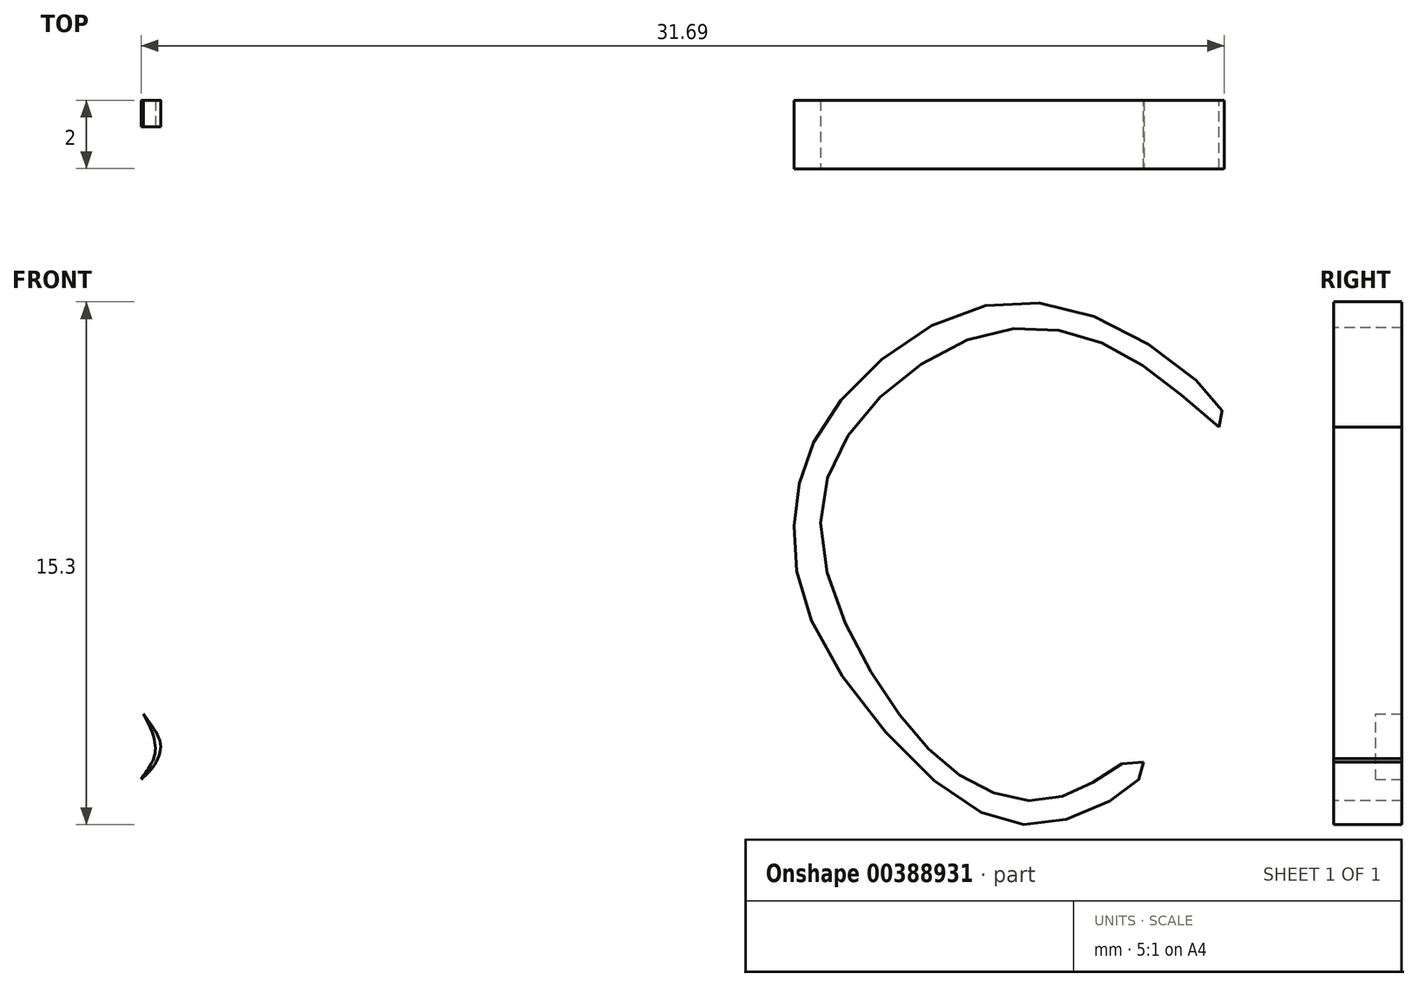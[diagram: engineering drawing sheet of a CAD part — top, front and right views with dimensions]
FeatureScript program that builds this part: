
annotation { "Feature Type Name" : "Feature", "Feature Type Description" : "" }
export const myFeature = defineFeature(function(context is Context, id is Id, definition is map)
    precondition{}
    {
        {
            var Q0;
            Q0=qCreatedBy(makeId("Front.planeOp"),FACE);
            var sketch = newSketch(context, id + "F0", { "sketchPlane" : qUnion([Q0])});
            skArc(sketch, "E0", {"start": v(-3.69, -6.27) * mm, "mid": v(-3.7, -6.14) * mm, "end": v(-3.75, -6.03) * mm});
            skArc(sketch, "E1", {"start": v(3.08, -7.56) * mm, "mid": v(3.43, -7.14) * mm, "end": v(3.75, -6.7) * mm});
            skArc(sketch, "E2", {"start": v(0.71, -7.74) * mm, "mid": v(1.48, -8.13) * mm, "end": v(2.34, -8.08) * mm});
            skArc(sketch, "E3", {"start": v(0.71, -7.74) * mm, "mid": v(-1.43, -7) * mm, "end": v(-3.66, -7.38) * mm});
            skArc(sketch, "E4", {"start": v(-3.75, -7.3) * mm, "mid": v(-3.7, -6.94) * mm, "end": v(-3.68, -6.58) * mm});
            skArc(sketch, "E5", {"start": v(-3.68, -6.58) * mm, "mid": v(-3.68, -6.42) * mm, "end": v(-3.69, -6.27) * mm});
            skArc(sketch, "E6", {"start": v(2.34, -8.08) * mm, "mid": v(2.75, -7.87) * mm, "end": v(3.08, -7.56) * mm});
            skArc(sketch, "E7", {"start": v(-3.75, -6.03) * mm, "mid": v(-3.11, -4.42) * mm, "end": v(-3.75, -2.81) * mm});
            skArc(sketch, "E8", {"start": v(-4.2, -1.47) * mm, "mid": v(-4.18, -2.2) * mm, "end": v(-3.75, -2.81) * mm});
            skArc(sketch, "E9", {"start": v(-4.2, -1.47) * mm, "mid": v(-4.23, -1.22) * mm, "end": v(-4.45, -1.12) * mm});
            skArc(sketch, "E10", {"start": v(-4.45, -1.12) * mm, "mid": v(-5.42, -1.46) * mm, "end": v(-6.03, -2.29) * mm});
            skArc(sketch, "E11", {"start": v(-6.03, -2.29) * mm, "mid": v(-6.03, -2.9) * mm, "end": v(-5.62, -3.34) * mm});
            skArc(sketch, "E12", {"start": v(-5.58, -3.48) * mm, "mid": v(-5.56, -3.4) * mm, "end": v(-5.62, -3.34) * mm});
            skArc(sketch, "E13", {"start": v(-5.85, -3.54) * mm, "mid": v(-5.7, -3.55) * mm, "end": v(-5.58, -3.48) * mm});
            skArc(sketch, "E14", {"start": v(-6.07, -3.4) * mm, "mid": v(-5.96, -3.48) * mm, "end": v(-5.85, -3.54) * mm});
            skArc(sketch, "E15", {"start": v(-6.07, -3.4) * mm, "mid": v(-6.2, -3.36) * mm, "end": v(-6.33, -3.4) * mm});
            skArc(sketch, "E16", {"start": v(-6.49, -3.4) * mm, "mid": v(-6.4, -3.43) * mm, "end": v(-6.33, -3.4) * mm});
            skArc(sketch, "E17", {"start": v(-6.49, -3.4) * mm, "mid": v(-6.53, -3.4) * mm, "end": v(-6.52, -3.45) * mm});
            skArc(sketch, "E18", {"start": v(-6.44, -3.64) * mm, "mid": v(-6.44, -3.53) * mm, "end": v(-6.52, -3.45) * mm});
            skArc(sketch, "E19", {"start": v(-6.94, -3.71) * mm, "mid": v(-6.68, -3.8) * mm, "end": v(-6.44, -3.64) * mm});
            skArc(sketch, "E20", {"start": v(-6.94, -3.71) * mm, "mid": v(-7, -3.7) * mm, "end": v(-7, -3.77) * mm});
            skArc(sketch, "E21", {"start": v(-6.83, -4.05) * mm, "mid": v(-6.89, -3.9) * mm, "end": v(-7, -3.77) * mm});
            skArc(sketch, "E22", {"start": v(-7, -4.29) * mm, "mid": v(-6.87, -4.2) * mm, "end": v(-6.83, -4.05) * mm});
            skArc(sketch, "E23", {"start": v(-8.44, -3.46) * mm, "mid": v(-7.85, -4.1) * mm, "end": v(-7, -4.29) * mm});
            skArc(sketch, "E24", {"start": v(-8.44, -3.46) * mm, "mid": v(-8.5, -3.42) * mm, "end": v(-8.58, -3.46) * mm});
            skArc(sketch, "E25", {"start": v(-8.58, -3.46) * mm, "mid": v(-8.6, -3.5) * mm, "end": v(-8.6, -3.53) * mm});
            skArc(sketch, "E26", {"start": v(-8.86, -3.73) * mm, "mid": v(-8.7, -3.67) * mm, "end": v(-8.6, -3.53) * mm});
            skArc(sketch, "E27", {"start": v(-10.15, -2.7) * mm, "mid": v(-9.7, -3.46) * mm, "end": v(-8.86, -3.73) * mm});
            skArc(sketch, "E28", {"start": v(-10.15, -1.95) * mm, "mid": v(-10.17, -2.33) * mm, "end": v(-10.15, -2.7) * mm});
            skArc(sketch, "E29", {"start": v(-10.15, -1.95) * mm, "mid": v(-10.19, -1.76) * mm, "end": v(-10.34, -1.64) * mm});
            skArc(sketch, "E30", {"start": v(-10.34, -1.64) * mm, "mid": v(-11.08, -1.57) * mm, "end": v(-11.81, -1.64) * mm});
            skArc(sketch, "E31", {"start": v(-11.81, -1.64) * mm, "mid": v(-12.01, -1.73) * mm, "end": v(-12.18, -1.88) * mm});
            skArc(sketch, "E32", {"start": v(-12.18, -1.88) * mm, "mid": v(-12.35, -2.1) * mm, "end": v(-12.51, -2.35) * mm});
            skArc(sketch, "E33", {"start": v(-13.94, -3.35) * mm, "mid": v(-13.1, -3.05) * mm, "end": v(-12.51, -2.35) * mm});
            skArc(sketch, "E34", {"start": v(-15.03, -2.58) * mm, "mid": v(-14.63, -3.17) * mm, "end": v(-13.94, -3.35) * mm});
            skArc(sketch, "E35", {"start": v(-14.95, -2.18) * mm, "mid": v(-15.04, -2.37) * mm, "end": v(-15.03, -2.58) * mm});
            skArc(sketch, "E36", {"start": v(-14.45, -1.64) * mm, "mid": v(-14.7, -1.9) * mm, "end": v(-14.95, -2.18) * mm});
            skArc(sketch, "E37", {"start": v(-14.45, -1.64) * mm, "mid": v(-14.26, -0.97) * mm, "end": v(-14.63, -0.38) * mm});
            skArc(sketch, "E38", {"start": v(-14.63, -0.38) * mm, "mid": v(-15.23, -0.4) * mm, "end": v(-15.62, -0.85) * mm});
            skArc(sketch, "E39", {"start": v(-16.04, -1.37) * mm, "mid": v(-15.79, -1.14) * mm, "end": v(-15.62, -0.85) * mm});
            skArc(sketch, "E40", {"start": v(-16.04, -1.37) * mm, "mid": v(-16.21, -1.5) * mm, "end": v(-16.36, -1.64) * mm});
            skArc(sketch, "E41", {"start": v(-17.02, -1.64) * mm, "mid": v(-16.69, -1.78) * mm, "end": v(-16.36, -1.64) * mm});
            skArc(sketch, "E42", {"start": v(-17.41, -1.23) * mm, "mid": v(-17.22, -1.44) * mm, "end": v(-17.02, -1.64) * mm});
            skArc(sketch, "E43", {"start": v(-17.89, 0.31) * mm, "mid": v(-17.85, -0.52) * mm, "end": v(-17.41, -1.23) * mm});
            skArc(sketch, "E44", {"start": v(-17.89, 0.31) * mm, "mid": v(-17.89, 0.33) * mm, "end": v(-17.9, 0.34) * mm});
            skArc(sketch, "E45", {"start": v(-17.9, 0.34) * mm, "mid": v(-17.94, 0.33) * mm, "end": v(-17.97, 0.3) * mm});
            skArc(sketch, "E46", {"start": v(-19.3, -0.58) * mm, "mid": v(-18.59, -0.2) * mm, "end": v(-17.97, 0.3) * mm});
            skArc(sketch, "E47", {"start": v(-19.9, -0.65) * mm, "mid": v(-19.6, -0.67) * mm, "end": v(-19.3, -0.58) * mm});
            skArc(sketch, "E48", {"start": v(-20.2, -0.11) * mm, "mid": v(-20.12, -0.42) * mm, "end": v(-19.9, -0.65) * mm});
            skArc(sketch, "E49", {"start": v(-20.2, -0.11) * mm, "mid": v(-20.18, 0.21) * mm, "end": v(-20.2, 0.54) * mm});
            skArc(sketch, "E50", {"start": v(-20.2, 0.54) * mm, "mid": v(-20.43, 1) * mm, "end": v(-20.9, 1.16) * mm});
            skArc(sketch, "E51", {"start": v(-20.9, 1.16) * mm, "mid": v(-22.68, 0.63) * mm, "end": v(-23.68, -0.94) * mm});
            skArc(sketch, "E52", {"start": v(-23.68, -0.94) * mm, "mid": v(-23.57, -1.58) * mm, "end": v(-23.11, -2.05) * mm});
            skArc(sketch, "E53", {"start": v(-22.81, -2.32) * mm, "mid": v(-22.93, -2.15) * mm, "end": v(-23.11, -2.05) * mm});
            skArc(sketch, "E54", {"start": v(-22.81, -2.6) * mm, "mid": v(-22.79, -2.45) * mm, "end": v(-22.81, -2.32) * mm});
            skArc(sketch, "E55", {"start": v(-23.7, -2.5) * mm, "mid": v(-23.28, -2.79) * mm, "end": v(-22.81, -2.6) * mm});
            skArc(sketch, "E56", {"start": v(-23.7, -2.5) * mm, "mid": v(-23.76, -2.37) * mm, "end": v(-23.84, -2.26) * mm});
            skArc(sketch, "E57", {"start": v(-23.84, -2.26) * mm, "mid": v(-23.93, -2.24) * mm, "end": v(-23.97, -2.32) * mm});
            skArc(sketch, "E58", {"start": v(-23.97, -2.32) * mm, "mid": v(-23.9, -2.69) * mm, "end": v(-23.68, -2.99) * mm});
            skArc(sketch, "E59", {"start": v(-23.63, -3.23) * mm, "mid": v(-23.6, -3.1) * mm, "end": v(-23.68, -2.99) * mm});
            skArc(sketch, "E60", {"start": v(-24.4, -3.23) * mm, "mid": v(-24.02, -3.39) * mm, "end": v(-23.63, -3.23) * mm});
            skArc(sketch, "E61", {"start": v(-24.4, -3.23) * mm, "mid": v(-24.46, -3.22) * mm, "end": v(-24.46, -3.28) * mm});
            skArc(sketch, "E62", {"start": v(-24.25, -3.83) * mm, "mid": v(-24.3, -3.54) * mm, "end": v(-24.46, -3.28) * mm});
            skArc(sketch, "E63", {"start": v(-24.88, -3.93) * mm, "mid": v(-24.52, -4.17) * mm, "end": v(-24.25, -3.83) * mm});
            skArc(sketch, "E64", {"start": v(-24.88, -3.93) * mm, "mid": v(-24.9, -3.83) * mm, "end": v(-24.92, -3.72) * mm});
            skArc(sketch, "E65", {"start": v(-24.92, -3.72) * mm, "mid": v(-24.98, -3.67) * mm, "end": v(-25.05, -3.72) * mm});
            skArc(sketch, "E66", {"start": v(-25.05, -3.72) * mm, "mid": v(-24.55, -5.28) * mm, "end": v(-23.07, -6) * mm});
            skArc(sketch, "E67", {"start": v(-23.07, -6) * mm, "mid": v(-22.64, -6) * mm, "end": v(-22.21, -6) * mm});
            skFitSpline(sketch, "E68", {"points": [v(-22.21, -6) * mm, v(-21.9, -5.69) * mm, v(-22.42, -5.12) * mm, v(-20.66, -4.08) * mm, v(-19.53, -4.6) * mm, v(-18.44, -3.59) * mm, v(-17.7, -3.55) * mm, v(-17.3, -4.07) * mm, v(-18.01, -5.15) * mm, v(-18.16, -6.77) * mm, v(-19.58, -7.9) * mm, v(-20.92, -8.76) * mm, v(-19.16, -9.38) * mm, v(-17.63, -11.12) * mm, v(-17.96, -11.4) * mm, v(-18.92, -11.12) * mm, v(-19.35, -11.4) * mm, v(-18.82, -12.21) * mm, v(-18.25, -13.86) * mm, v(-17.89, -14.27) * mm, v(-17.26, -14.18) * mm, v(-17.21, -14.1) * mm, v(-16.82, -13.65) * mm, v(-16.4, -14.93) * mm, v(-15.95, -16.13) * mm, v(-16, -16.67) * mm, v(-16.88, -17.28) * mm, v(-18, -17) * mm, v(-18.67, -16.4) * mm, v(-18.87, -16.58) * mm, v(-20.13, -18.4) * mm, v(-22.21, -18.16) * mm, v(-23.39, -16.7) * mm, v(-22.8, -16) * mm, v(-22.6, -15.5) * mm, v(-21.4, -14.67) * mm, v(-20.45, -15.27) * mm, v(-20.4, -15.2) * mm, v(-19.55, -14.57) * mm, v(-19.55, -14.51) * mm, v(-20.24, -12.1) * mm, v(-21.74, -9.86) * mm, v(-21.89, -10) * mm, v(-22.57, -11.73) * mm, v(-24.55, -12.05) * mm, v(-25.57, -11.22) * mm, v(-25.52, -10.76) * mm, v(-24.63, -10.83) * mm, v(-23.99, -10.75) * mm, v(-23.57, -10.3) * mm, v(-23.62, -9.63) * mm, v(-24.39, -9.1) * mm, v(-24.85, -8.06) * mm, v(-24.99, -7.7) * mm, v(-25.33, -7.6) * mm, v(-25.79, -8.16) * mm, v(-26.7, -8.35) * mm, v(-26.98, -8) * mm, v(-26.47, -7.58) * mm, v(-25.9, -6.57) * mm, v(-26.59, -5.35) * mm, v(-26.9, -3.41) * mm, v(-26.66, -1.41) * mm, v(-26.1, -0.15) * mm, v(-26.15, -0.1) * mm, v(-26.98, -0.1) * mm, v(-27.86, 1) * mm, v(-27.19, 1.9) * mm, v(-26.36, 1.09) * mm, v(-25.57, 0.89) * mm, v(-24.93, 1.43) * mm, v(-25.03, 2.07) * mm, v(-24.98, 2.4) * mm, v(-24.52, 2.24) * mm, v(-23.77, 2.17) * mm, v(-23.28, 2.53) * mm, v(-23.85, 3.22) * mm, v(-24.88, 4.71) * mm, v(-25.1, 6.85) * mm, v(-24.19, 7.52) * mm, v(-23.42, 7.55) * mm, v(-23.42, 7.81) * mm, v(-22.98, 7.98) * mm, v(-22.02, 7) * mm, v(-21.13, 6.22) * mm, v(-20.8, 6.59) * mm, v(-20.77, 6.92) * mm, v(-20.34, 7.57) * mm, v(-19.35, 7.23) * mm, v(-19.43, 6.54) * mm, v(-19.19, 6) * mm, v(-18.92, 6.15) * mm, v(-18.73, 6.59) * mm, v(-17.48, 5.5) * mm, v(-17.65, 4.85) * mm, v(-17.53, 4.1) * mm, v(-16.28, 3.5) * mm, v(-15.58, 4.1) * mm, v(-15.99, 5.29) * mm, v(-16.18, 7.76) * mm, v(-14.98, 10.1) * mm, v(-14.02, 10.84) * mm, v(-14.04, 10.98) * mm, v(-14.3, 11.2) * mm, v(-14.26, 11.68) * mm, v(-14.9, 12.35) * mm, v(-14.47, 12.76) * mm, v(-14.5, 12.98) * mm, v(-13.31, 13.17) * mm, v(-12.95, 12.98) * mm, v(-12.78, 12.7) * mm, v(-12.5, 12.73) * mm, v(-12.51, 11.57) * mm, v(-12.8, 11.39) * mm, v(-12.87, 11.15) * mm, v(-12.56, 10.86) * mm, v(-12.17, 11.28) * mm, v(-12.07, 11.93) * mm, v(-11.4, 12.97) * mm, v(-10.5, 12.27) * mm, v(-10.81, 11.25) * mm, v(-11.37, 10.8) * mm, v(-11.37, 10.2) * mm, v(-10.6, 9.47) * mm, v(-10.71, 7.65) * mm, v(-11.88, 7.07) * mm, v(-12.68, 7.83) * mm, v(-12.61, 8.84) * mm, v(-12.09, 8.94) * mm, v(-11.99, 8.56) * mm, v(-12.3, 8.34) * mm, v(-12.41, 8.1) * mm, v(-11.92, 7.99) * mm, v(-11.6, 8.77) * mm, v(-11.88, 9.26) * mm, v(-12.97, 9.2) * mm, v(-13.24, 8.02) * mm, v(-12.78, 7.4) * mm, v(-12.99, 7.05) * mm, v(-13.52, 7.56) * mm, v(-13.52, 8.22) * mm, v(-13.79, 8.07) * mm, v(-13.75, 7.4) * mm, v(-13.5, 7.2) * mm, v(-13.74, 6.83) * mm, v(-13.7, 5.91) * mm, v(-13.1, 5.64) * mm, v(-12.67, 6.13) * mm, v(-12.34, 6.25) * mm, v(-12.17, 5.76) * mm, v(-12.27, 5.27) * mm, v(-11.88, 4.76) * mm, v(-11.05, 4.98) * mm, v(-10.8, 4.8) * mm, v(-11.14, 3.82) * mm, v(-10.97, 1.97) * mm, v(-9.55, 0.66) * mm, v(-8.25, 0.7) * mm, v(-7.67, 1.44) * mm, v(-7.7, 2.05) * mm, v(-7.2, 2.2) * mm, v(-7.14, 2.45) * mm, v(-6.68, 2.43) * mm, v(-6.73, 2.87) * mm, v(-6, 3.16) * mm, v(-6.05, 3.53) * mm, v(-5.3, 3.55) * mm, v(-5.16, 3.86) * mm, v(-4.16, 3.78) * mm, v(-3.69, 4.3) * mm, v(-2.67, 4.26) * mm, v(-2.26, 4.35) * mm, v(-2.19, 4.83) * mm, v(-1.73, 4.9) * mm, v(-1.64, 5.52) * mm, v(-2.17, 6.6) * mm, v(-2.43, 7.76) * mm, v(-3.17, 8.62) * mm, v(-3.99, 9.16) * mm, v(-3.79, 9.72) * mm, v(-2.96, 9.77) * mm, v(-2.77, 10.18) * mm, v(-1.46, 10.34) * mm, v(-1.13, 10.32) * mm, v(-1.07, 10.64) * mm, v(-0.66, 10.82) * mm, v(-0.53, 11.1) * mm, v(-0.66, 11.45) * mm, v(-0.53, 11.92) * mm, v(-0.62, 12.39) * mm, v(-1, 12.6) * mm, v(-1.12, 13.07) * mm, v(-1.87, 13.16) * mm, v(-2.38, 13.87) * mm, v(-2.16, 14.67) * mm, v(-2.29, 15.23) * mm, v(-2.8, 15.72) * mm, v(-2.88, 16.93) * mm, v(-2.36, 17.1) * mm, v(-2.01, 18.05) * mm, v(-1.15, 18.93) * mm, v(-1.23, 19.93) * mm, v(-0.72, 20.85) * mm, v(0.24, 20.64) * mm, v(0.5, 19.89) * mm, v(0.83, 19.65) * mm, v(1.03, 20.22) * mm, v(1.62, 20.54) * mm, v(1.85, 21) * mm, v(1.8, 21.4) * mm, v(2.12, 21.8) * mm, v(2.42, 21.23) * mm, v(3.19, 20.8) * mm, v(3.2, 20.38) * mm, v(2.52, 20.42) * mm, v(3.1, 19.8) * mm, v(3.13, 19.02) * mm, v(3.53, 18.64) * mm, v(4.12, 18.7) * mm, v(4.51, 18.33) * mm, v(4.52, 18.01) * mm, v(4.78, 17.78) * mm, v(4.97, 17.45) * mm, v(4.72, 17.03) * mm, v(4.3, 17.17) * mm, v(4.45, 16.92) * mm, v(4.54, 16.54) * mm, v(3.13, 15.18) * mm, v(2.28, 14.96) * mm, v(0.66, 13.16) * mm, v(0.76, 13.02) * mm, v(1.03, 12.76) * mm, v(0.88, 12.47) * mm, v(0.92, 12.05) * mm, v(1.37, 11.9) * mm, v(1.35, 11.58) * mm, v(1.33, 10.63) * mm, v(1.7, 10.73) * mm, v(1.98, 10.37) * mm, v(2.16, 10.19) * mm, v(2.4, 10.37) * mm, v(3.41, 10.27) * mm, v(3.73, 9.64) * mm, v(4.08, 9.72) * mm, v(4.74, 9.68) * mm, v(4.97, 8.61) * mm, v(4.57, 8.22) * mm, v(4.03, 8.32) * mm, v(3.72, 8.02) * mm, v(3.54, 7.54) * mm, v(3.18, 7.18) * mm, v(2.23, 5.35) * mm, v(2.39, 4.4) * mm, v(3.11, 4.19) * mm, v(4.08, 3.58) * mm, v(4.8, 3.55) * mm, v(5.54, 3) * mm, v(5.5, 2.69) * mm, v(5.8, 2.47) * mm, v(7.01, 2.48) * mm, v(7.32, 2.07) * mm, v(7.84, 2) * mm, v(8.06, 1.4) * mm, v(7.9, 1.06) * mm, v(7.96, 0.8) * mm, v(8.38, 0.7) * mm, v(8.6, -0.11) * mm, v(10.91, 0.96) * mm, v(11.66, 2.74) * mm, v(11.15, 3.49) * mm, v(10.93, 4.07) * mm, v(11.8, 4.33) * mm, v(12.5, 3.73) * mm, v(12.69, 3.97) * mm, v(12.73, 4.6) * mm, v(13.15, 4.66) * mm, v(13.15, 5.37) * mm, v(13.6, 5.79) * mm, v(14.02, 4.9) * mm, v(14.19, 5.37) * mm, v(14.49, 5.12) * mm, v(14.6, 6.05) * mm, v(13.86, 6.78) * mm, v(13.68, 6.64) * mm, v(12.65, 6.05) * mm, v(11.52, 6.4) * mm, v(10.95, 7.8) * mm, v(11.66, 9.23) * mm, v(12.18, 9.6) * mm, v(12.29, 10.18) * mm, v(11.98, 10.32) * mm, v(11.78, 10.03) * mm, v(11.54, 10.6) * mm, v(11.72, 12) * mm, v(12.59, 12.4) * mm, v(13.28, 11.71) * mm, v(13.68, 11.35) * mm, v(14.1, 12) * mm, v(15.28, 12.38) * mm, v(16.4, 11.6) * mm, v(16.29, 11.27) * mm, v(15.58, 11.27) * mm, v(15.48, 10.98) * mm, v(15.3, 10.66) * mm, v(15.14, 10.24) * mm, v(15.48, 9.45) * mm], "startDerivative": vector(210.1, 118.94) * mm, "endDerivative": vector(144.38, -239.42) * mm});
            skFitSpline(sketch, "E69", {"points": [v(15.48, 9.45) * mm, v(16.8, 7.3) * mm, v(16.96, 5.4) * mm, v(16.3, 3.59) * mm, v(16.35, 3.18) * mm, v(16.85, 3.1) * mm, v(17.08, 2.8) * mm, v(17.12, 2.56) * mm, v(17.42, 2.7) * mm, v(18.09, 3.7) * mm, v(18.29, 5.04) * mm, v(18.86, 5.75) * mm, v(19.46, 5.33) * mm, v(19.64, 5.02) * mm, v(20.19, 6.03) * mm, v(21.24, 7.1) * mm, v(21.77, 6.62) * mm, v(21.56, 5.95) * mm, v(21.58, 4.92) * mm, v(22.13, 5.08) * mm, v(22.66, 5.08) * mm, v(22.98, 5.69) * mm, v(23.5, 6.01) * mm, v(23.74, 6.45) * mm, v(24.53, 6.73) * mm, v(25.91, 5.3) * mm, v(25.5, 2.83) * mm, v(24.31, 1.79) * mm, v(24.24, 1.39) * mm, v(24.9, 0.9) * mm, v(25.83, -0.16) * mm, v(26.79, -0.67) * mm, v(27.53, -0.46) * mm, v(27.59, 0.06) * mm, v(27.42, 0.32) * mm, v(27.64, 0.67) * mm, v(28.32, -0.13) * mm, v(28.46, -2) * mm, v(27.46, -2.76) * mm, v(26.82, -2.67) * mm, v(26.94, -3.27) * mm, v(27.4, -4.6) * mm, v(27.24, -6.37) * mm, v(26.67, -7.12) * mm, v(26.47, -8.23) * mm, v(26.74, -8.55) * mm, v(26.46, -8.92) * mm, v(26.66, -9.53) * mm, v(27.3, -9.55) * mm, v(27.53, -9.82) * mm, v(26.82, -10.26) * mm, v(25.67, -9.92) * mm, v(25.44, -9.6) * mm, v(25.03, -10) * mm, v(24.01, -10.56) * mm, v(23.93, -11.56) * mm, v(24.74, -12.2) * mm, v(25.59, -11.96) * mm, v(25.93, -12.22) * mm, v(24.21, -13.7) * mm, v(23.4, -14) * mm, v(22.46, -13.52) * mm, v(21.88, -13.18) * mm, v(21.24, -13.52) * mm, v(19.67, -15.94) * mm, v(20.03, -16.27) * mm, v(21.33, -16.04) * mm, v(22.48, -16.32) * mm, v(23.26, -17.58) * mm, v(22.53, -19.4) * mm, v(20.98, -20.28) * mm, v(19.08, -19.65) * mm, v(18.52, -18.7) * mm, v(18.45, -17.92) * mm, v(18.02, -17.58) * mm, v(17.41, -18) * mm, v(17.08, -18) * mm, v(16.84, -17.54) * mm, v(16.64, -17.5) * mm, v(16.34, -17.42) * mm, v(16.22, -16.8) * mm, v(16.47, -16.58) * mm, v(16.27, -16.27) * mm, v(16.45, -15.95) * mm, v(16.64, -16.1) * mm, v(16.85, -15.76) * mm, v(16.5, -15.26) * mm, v(16.98, -14.94) * mm, v(17.44, -15.15) * mm, v(18.85, -13.62) * mm, v(19.01, -12.48) * mm, v(18.65, -12.12) * mm, v(18.15, -12.53) * mm, v(17.41, -12.5) * mm, v(17.54, -11.98) * mm, v(18, -11.68) * mm, v(17.91, -11.3) * mm, v(18.31, -11.12) * mm, v(18.57, -10.9) * mm, v(18.57, -10.25) * mm, v(18.98, -10.28) * mm, v(19.93, -10.63) * mm, v(21.2, -10.3) * mm, v(20.98, -9.68) * mm, v(19.23, -8.79) * mm, v(18.62, -8.26) * mm, v(18.54, -6.5) * mm, v(18.52, -5.52) * mm, v(18.12, -5.27) * mm, v(17.9, -4.97) * mm, v(18.17, -4.52) * mm, v(19, -4.74) * mm, v(19.31, -5.43) * mm, v(19.53, -5.69) * mm, v(19.73, -5.16) * mm, v(20.24, -5.09) * mm, v(20.6, -4.7) * mm, v(21.33, -5.04) * mm, v(22.04, -5.2) * mm, v(22.27, -6) * mm, v(22.06, -6.47) * mm, v(22.46, -7.06) * mm, v(23.74, -6.43) * mm, v(25.24, -4.79) * mm, v(25.14, -4.37) * mm, v(24.71, -4.13) * mm, v(23.97, -4.29) * mm, v(23.3, -4.04) * mm, v(23.37, -3.62) * mm, v(23.88, -3.19) * mm, v(23.21, -1.7) * mm, v(22.06, -0.56) * mm, v(21.31, -0.54) * mm, v(21, -0.96) * mm, v(21.15, -1.57) * mm, v(20.74, -1.94) * mm, v(19.8, -1.86) * mm, v(18.6, -1.21) * mm, v(17.98, -1.06) * mm, v(17.9, -1.66) * mm, v(17.75, -2) * mm, v(17.47, -2.04) * mm, v(15.95, -1.6) * mm, v(15.05, -1.03) * mm, v(14.08, -0.97) * mm, v(13.44, -1.43) * mm, v(14.14, -2.04) * mm, v(15.24, -2.74) * mm, v(15.77, -3.39) * mm, v(15, -3.63) * mm, v(13.15, -3.49) * mm, v(12.06, -2.53) * mm, v(11.76, -1.71) * mm, v(11.28, -1.37) * mm, v(10.53, -1.99) * mm, v(10.3, -3) * mm, v(10.28, -3.82) * mm, v(9.66, -3.83) * mm, v(9.1, -3.29) * mm, v(8.73, -3.69) * mm, v(8.1, -4.29) * mm, v(7.76, -4.46) * mm, v(7.2, -3.77) * mm, v(7.1, -3.27) * mm, v(6.72, -3.59) * mm, v(6.29, -3.86) * mm, v(6, -3.32) * mm, v(6.08, -2.39) * mm, v(5.66, -1.84) * mm, v(4.72, -1.57) * mm, v(2.79, -2.17) * mm, v(1.92, -3.89) * mm, v(2.23, -5.47) * mm, v(3.36, -6.65) * mm, v(3.75, -6.7) * mm], "startDerivative": vector(154.8, -214.57) * mm, "endDerivative": vector(87.05, 10.6) * mm});
            skFitSpline(sketch, "E70", {"points": [v(-1.09, -4.51) * mm, v(-1.2, -4.56) * mm, v(-1.23, -5.16) * mm, v(-1.76, -6.02) * mm, v(-2.78, -6.35) * mm, v(-2.88, -6.46) * mm, v(-2.78, -6.65) * mm, v(-1.6, -6.22) * mm, v(-0.98, -5.4) * mm, v(-0.91, -4.6) * mm, v(-1.09, -4.51) * mm]});
            skFitSpline(sketch, "E71", {"points": [v(-0.08, -4.47) * mm, v(-0.25, -4.57) * mm, v(-0.31, -5.7) * mm, v(0.17, -6.76) * mm, v(1.03, -7.55) * mm, v(1.27, -7.53) * mm, v(1.28, -7.35) * mm, v(0.55, -6.77) * mm, v(-0.07, -5.26) * mm, v(0.14, -4.63) * mm, v(-0.08, -4.47) * mm]});
            skFitSpline(sketch, "E72", {"points": [v(1.1, -2.72) * mm, v(1.06, -2.9) * mm, v(0.2, -3.37) * mm, v(-0.9, -3.19) * mm, v(-2.58, -1.25) * mm, v(-2.82, 0.09) * mm, v(-2.44, 1.18) * mm, v(-0.9, 2.36) * mm, v(0.85, 2.16) * mm, v(2, 1.2) * mm, v(1.95, 1.05) * mm], "startDerivative": vector(0.31, -4.22) * mm, "endDerivative": vector(-3.07, -3.26) * mm});
            skFitSpline(sketch, "E73", {"points": [v(1.95, 1.05) * mm, v(0.67, 1.98) * mm, v(-0.68, 2.1) * mm, v(-2.13, 1.09) * mm, v(-2.52, -0.28) * mm, v(-1.75, -2.04) * mm, v(-0.87, -2.93) * mm, v(-0.02, -3.15) * mm, v(0.68, -2.85) * mm, v(1.1, -2.72) * mm], "startDerivative": vector(-9.7, 8.55) * mm, "endDerivative": vector(3.66, -4.58) * mm});
            skFitSpline(sketch, "E74", {"points": [v(-0.55, -0.47) * mm, v(-0.54, -0.65) * mm, v(-1.62, -0.71) * mm, v(-2.06, -0.38) * mm, v(-2.08, 0.56) * mm, v(-1.25, 1.4) * mm, v(-0.61, 1.47) * mm, v(-0.5, 1.26) * mm, v(-0.81, 1.2) * mm, v(-1.42, 1) * mm, v(-1.86, 0.33) * mm, v(-1.71, -0.38) * mm, v(-1.01, -0.46) * mm, v(-0.55, -0.47) * mm]});
            skFitSpline(sketch, "E75", {"points": [v(0.27, -0.52) * mm, v(0.3, -0.67) * mm, v(0.8, -0.73) * mm, v(2.4, -0.7) * mm, v(2.66, -0.5) * mm, v(2.44, -0.16) * mm, v(1.45, 0.78) * mm, v(0.36, 1.3) * mm, v(0.29, 1.14) * mm, v(0.51, 1.04) * mm, v(1.86, 0.15) * mm, v(2.4, -0.38) * mm, v(2.35, -0.46) * mm, v(0.5, -0.42) * mm, v(0.27, -0.52) * mm]});
            skFitSpline(sketch, "E76", {"points": [v(2.51, 1.91) * mm, v(2.5, 1.8) * mm, v(4.1, 0.16) * mm, v(5.83, -1.16) * mm, v(6.1, -1.22) * mm, v(6.11, -1.1) * mm, v(5.78, -0.87) * mm, v(4.31, 0.24) * mm, v(2.98, 1.58) * mm, v(2.64, 1.98) * mm, v(2.51, 1.91) * mm]});
            skFitSpline(sketch, "E77", {"points": [v(4.13, 1.99) * mm, v(3.97, 1.91) * mm, v(5.08, 0.67) * mm, v(6.37, -0.32) * mm, v(6.6, -0.32) * mm, v(6.6, -0.13) * mm, v(6.48, -0.09) * mm, v(5.2, 0.9) * mm, v(4.3, 1.94) * mm, v(4.13, 1.99) * mm]});
            skFitSpline(sketch, "E78", {"points": [v(1.85, 2.75) * mm, v(1.86, 2.88) * mm, v(2.58, 3.16) * mm, v(4.22, 3.11) * mm, v(4.83, 2.88) * mm, v(4.75, 2.7) * mm, v(4.2, 2.87) * mm, v(2.66, 2.9) * mm, v(1.85, 2.75) * mm]});
            skFitSpline(sketch, "E79", {"points": [v(7.08, 1.97) * mm, v(7.19, 1.84) * mm, v(6.92, 1.56) * mm, v(6.62, 1.66) * mm, v(6.7, 1.82) * mm, v(6.92, 1.83) * mm, v(7.08, 1.97) * mm]});
            skFitSpline(sketch, "E80", {"points": [v(6.31, 1.73) * mm, v(6.33, 1.52) * mm, v(5.63, 1.63) * mm, v(5.2, 1.93) * mm, v(5.22, 2.21) * mm, v(5.37, 2.1) * mm, v(5.83, 1.83) * mm, v(6.31, 1.73) * mm]});
            skFitSpline(sketch, "E81", {"points": [v(-0.6, 3.08) * mm, v(-0.42, 3.1) * mm, v(-0.34, 3.5) * mm, v(0.05, 4.15) * mm, v(0.78, 4.48) * mm, v(1.14, 4.45) * mm, v(1.21, 4.68) * mm, v(0.95, 4.73) * mm, v(0.3, 4.58) * mm, v(-0.46, 3.88) * mm, v(-0.6, 3.08) * mm]});
            skFitSpline(sketch, "E82", {"points": [v(-2.2, 3.49) * mm, v(-2.1, 3.37) * mm, v(-1.88, 3.65) * mm, v(-1.2, 4.34) * mm, v(-0.36, 4.74) * mm, v(-0.23, 4.89) * mm, v(-0.37, 5) * mm, v(-1.52, 4.38) * mm, v(-2.2, 3.49) * mm]});
            skFitSpline(sketch, "E83", {"points": [v(-0.46, 5.42) * mm, v(-0.34, 5.42) * mm, v(-0.33, 6.15) * mm, v(-0.9, 7.93) * mm, v(-1.74, 9.14) * mm, v(-1.93, 9.22) * mm, v(-1.87, 9.01) * mm, v(-1.18, 8) * mm, v(-0.62, 6.27) * mm, v(-0.46, 5.42) * mm]});
            skFitSpline(sketch, "E84", {"points": [v(-0.79, 9.67) * mm, v(-0.6, 9.61) * mm, v(-0.4, 9.16) * mm, v(0.27, 8.77) * mm, v(0.95, 9.18) * mm, v(1.07, 9.73) * mm, v(1.4, 9.6) * mm, v(0.74, 8.65) * mm, v(-0.15, 8.57) * mm, v(-0.73, 9.14) * mm, v(-0.79, 9.67) * mm]});
            skFitSpline(sketch, "E85", {"points": [v(2.15, 9.67) * mm, v(2.25, 9.48) * mm, v(2.06, 9.28) * mm, v(1.17, 7.67) * mm, v(0.8, 5.62) * mm, v(0.66, 5.4) * mm, v(0.54, 5.5) * mm, v(0.85, 7.75) * mm, v(2.15, 9.67) * mm]});
            skFitSpline(sketch, "E86", {"points": [v(1.3, 5.03) * mm, v(1.23, 5.3) * mm, v(1.97, 7.33) * mm, v(3.12, 9.2) * mm, v(3.35, 9.16) * mm, v(3.24, 8.93) * mm, v(2.17, 7.25) * mm, v(1.52, 5.21) * mm, v(1.3, 5.03) * mm]});
            skFitSpline(sketch, "E87", {"points": [v(-6.84, 0.9) * mm, v(-6.67, 1.1) * mm, v(-6.3, 0.99) * mm, v(-4.33, 1.46) * mm, v(-3.08, 2.72) * mm, v(-2.8, 2.95) * mm, v(-2.74, 2.81) * mm, v(-4.16, 1.22) * mm, v(-6.84, 0.9) * mm]});
            skFitSpline(sketch, "E88", {"points": [v(-6.28, -0.29) * mm, v(-6.05, -0.45) * mm, v(-6.25, -0.61) * mm, v(-6.96, -0.85) * mm, v(-7.3, -1.55) * mm, v(-7.49, -1.7) * mm, v(-7.6, -1.52) * mm, v(-7.19, -0.65) * mm, v(-6.28, -0.29) * mm]});
            skFitSpline(sketch, "E89", {"points": [v(-8.79, -3.17) * mm, v(-9, -2.6) * mm, v(-9.02, -1.95) * mm, v(-8.84, -1.83) * mm, v(-8.75, -2.03) * mm, v(-8.7, -2.55) * mm, v(-8.54, -3.05) * mm, v(-8.58, -3.17) * mm, v(-8.79, -3.17) * mm]});
            skFitSpline(sketch, "E90", {"points": [v(-7.6, -2.3) * mm, v(-7.43, -2.4) * mm, v(-7.33, -3) * mm, v(-7.08, -3.47) * mm, v(-7.17, -3.62) * mm, v(-7.59, -3.04) * mm, v(-7.6, -2.3) * mm]});
            skFitSpline(sketch, "E91", {"points": [v(-6.64, -3.17) * mm, v(-6.97, -2.88) * mm, v(-6.98, -2.59) * mm, v(-6.8, -2.75) * mm, v(-6.6, -3) * mm, v(-6.64, -3.17) * mm]});
            skFitSpline(sketch, "E92", {"points": [v(-11.12, -0.31) * mm, v(-10.94, -0.24) * mm, v(-11.03, -0.03) * mm, v(-12.18, 0.21) * mm, v(-13.28, -0.01) * mm, v(-13.38, -0.25) * mm, v(-13.15, -0.34) * mm, v(-12.13, -0.07) * mm, v(-11.12, -0.31) * mm]});
            skFitSpline(sketch, "E93", {"points": [v(-13.72, 4.93) * mm, v(-13.5, 4.7) * mm, v(-13.3, 3.45) * mm, v(-11.76, 1.2) * mm, v(-10.38, 0.43) * mm, v(-10.4, 0.15) * mm, v(-11.92, 1) * mm, v(-13.61, 3.38) * mm, v(-13.72, 4.93) * mm]});
            skFitSpline(sketch, "E94", {"points": [v(-15, 2.95) * mm, v(-14.83, 2.95) * mm, v(-13.64, 1.58) * mm, v(-12.1, 0.7) * mm, v(-11.98, 0.51) * mm, v(-12.16, 0.45) * mm, v(-13.8, 1.43) * mm, v(-15, 2.95) * mm]});
            skFitSpline(sketch, "E95", {"points": [v(-15.1, 4.24) * mm, v(-14.86, 4.18) * mm, v(-14.82, 4.43) * mm, v(-15.3, 6.32) * mm, v(-14.4, 8.95) * mm, v(-12.53, 9.99) * mm, v(-12.4, 10.14) * mm, v(-12.59, 10.31) * mm, v(-14.57, 9.13) * mm, v(-15.58, 6.36) * mm, v(-15.1, 4.24) * mm]});
            skFitSpline(sketch, "E96", {"points": [v(-17.82, 0.47) * mm, v(-17.16, 1.05) * mm, v(-17, 1.11) * mm, v(-16.96, 0.91) * mm, v(-17.82, 0.47) * mm]});
            skFitSpline(sketch, "E97", {"points": [v(-14.63, 1.2) * mm, v(-14.4, 1.24) * mm, v(-14.5, 1.47) * mm, v(-15.83, 1.89) * mm, v(-18.44, 3.44) * mm, v(-19.48, 4.38) * mm, v(-19.75, 4.4) * mm, v(-19.65, 4.2) * mm, v(-18.36, 3.03) * mm, v(-15.9, 1.62) * mm, v(-14.63, 1.2) * mm]});
            skFitSpline(sketch, "E98", {"points": [v(-20.56, 4.12) * mm, v(-20.37, 4.08) * mm, v(-19.54, 3.02) * mm, v(-18.21, 2.21) * mm, v(-18.1, 1.98) * mm, v(-18.4, 1.94) * mm, v(-20.26, 3.5) * mm, v(-20.56, 4.12) * mm]});
            skFitSpline(sketch, "E99", {"points": [v(-20.63, 4.76) * mm, v(-20.6, 4.71) * mm, v(-20.44, 4.78) * mm, v(-20.51, 4.92) * mm, v(-20.5, 5.36) * mm, v(-20.17, 5.47) * mm, v(-20.06, 5.3) * mm, v(-19.98, 5.36) * mm, v(-20.05, 5.7) * mm, v(-20.7, 5.52) * mm, v(-20.63, 4.76) * mm]});
            skFitSpline(sketch, "E100", {"points": [v(-21.45, 4.47) * mm, v(-21.24, 4.45) * mm, v(-21.2, 4.56) * mm, v(-21.3, 4.8) * mm, v(-21.25, 5.4) * mm, v(-20.84, 5.73) * mm, v(-20.92, 5.97) * mm, v(-21.57, 5.4) * mm, v(-21.45, 4.47) * mm]});
            skFitSpline(sketch, "E101", {"points": [v(-23.56, 5.11) * mm, v(-23.33, 5.06) * mm, v(-23.11, 4.6) * mm, v(-22.38, 3.97) * mm, v(-21.38, 3.96) * mm, v(-21.08, 3.95) * mm, v(-21.21, 3.7) * mm, v(-22.32, 3.72) * mm, v(-23.3, 4.4) * mm, v(-23.56, 5.11) * mm]});
            skFitSpline(sketch, "E102", {"points": [v(-22.98, 7.12) * mm, v(-22.85, 6.94) * mm, v(-23.04, 6.77) * mm, v(-23.54, 6.78) * mm, v(-24.04, 6.17) * mm, v(-23.83, 4.81) * mm, v(-22.97, 3.62) * mm, v(-22.03, 3.1) * mm, v(-22.07, 2.88) * mm, v(-23, 3.32) * mm, v(-24.04, 4.63) * mm, v(-24.39, 5.76) * mm, v(-23.95, 6.9) * mm, v(-22.98, 7.12) * mm]});
            skFitSpline(sketch, "E103", {"points": [v(-21.19, 2.6) * mm, v(-20.91, 2.62) * mm, v(-20.88, 2.28) * mm, v(-21.64, 2.17) * mm, v(-23.53, 1.09) * mm, v(-24.85, -0.72) * mm, v(-25.1, -1.26) * mm, v(-25.33, -1.08) * mm, v(-24.7, 0.11) * mm, v(-22.6, 2.13) * mm, v(-21.19, 2.6) * mm]});
            skFitSpline(sketch, "E104", {"points": [v(-24.96, -1.85) * mm, v(-24.75, -2) * mm, v(-24.75, -2.46) * mm, v(-24.55, -2.99) * mm, v(-24.73, -3.16) * mm, v(-25.03, -2.45) * mm, v(-24.96, -1.85) * mm]});
            skFitSpline(sketch, "E105", {"points": [v(-25.74, -2.01) * mm, v(-25.54, -2.23) * mm, v(-25.68, -2.6) * mm, v(-25.62, -4.41) * mm, v(-24.55, -6.1) * mm, v(-23.03, -6.9) * mm, v(-21.5, -6.9) * mm, v(-21.1, -6.99) * mm, v(-21.43, -7.2) * mm, v(-23.2, -7.17) * mm, v(-24.85, -6.16) * mm, v(-25.33, -5.61) * mm, v(-25.33, -6.57) * mm, v(-25.8, -7.39) * mm, v(-26.4, -7.96) * mm, v(-25.82, -7.04) * mm, v(-25.65, -6.07) * mm, v(-25.65, -5.26) * mm, v(-26, -4.33) * mm, v(-26, -2.96) * mm, v(-25.74, -2.01) * mm]});
            skFitSpline(sketch, "E106", {"points": [v(-24.72, -7.27) * mm, v(-24.62, -7.04) * mm, v(-23.35, -8.47) * mm, v(-22.7, -10.22) * mm, v(-23.1, -11.25) * mm, v(-23.82, -11.55) * mm, v(-24.18, -11.29) * mm, v(-23.9, -11.22) * mm, v(-23.42, -11.2) * mm, v(-22.98, -10.57) * mm, v(-23.2, -9.2) * mm, v(-24, -7.96) * mm, v(-24.72, -7.27) * mm]});
            skFitSpline(sketch, "E107", {"points": [v(-23.1, -7.8) * mm, v(-22.9, -7.97) * mm, v(-21.4, -7.94) * mm, v(-19.52, -6.9) * mm, v(-18.77, -5.9) * mm, v(-18.73, -4.94) * mm, v(-19.06, -5) * mm, v(-18.99, -5.69) * mm, v(-19.42, -6.4) * mm, v(-19.4, -5.96) * mm, v(-19.95, -5.16) * mm, v(-20.92, -4.99) * mm, v(-20.92, -5.26) * mm, v(-20.38, -5.23) * mm, v(-19.73, -5.77) * mm, v(-19.73, -6.54) * mm, v(-20.65, -7.42) * mm, v(-22.42, -7.72) * mm, v(-22.92, -7.6) * mm, v(-23.1, -7.8) * mm]});
            skFitSpline(sketch, "E108", {"points": [v(-21.48, -15.38) * mm, v(-22, -15.75) * mm, v(-21.93, -16.53) * mm, v(-21.12, -16.82) * mm, v(-20.98, -17.06) * mm, v(-21.6, -17.12) * mm, v(-22.3, -16.5) * mm, v(-22.28, -15.62) * mm, v(-21.55, -15.18) * mm, v(-21.48, -15.38) * mm]});
            skFitSpline(sketch, "E109", {"points": [v(-20.75, -15.5) * mm, v(-20.96, -16.13) * mm, v(-20.75, -17.06) * mm, v(-20.36, -17.4) * mm, v(-20.3, -17.2) * mm, v(-20.66, -16.56) * mm, v(-20.55, -15.75) * mm, v(-20.75, -15.5) * mm]});
            skFitSpline(sketch, "E110", {"points": [v(-17.47, -14.55) * mm, v(-17.39, -15.2) * mm, v(-16.8, -15.8) * mm, v(-16.75, -15.58) * mm, v(-17.06, -15.2) * mm, v(-17.12, -14.6) * mm, v(-17.47, -14.55) * mm]});
            skFitSpline(sketch, "E111", {"points": [v(-1.82, 15.44) * mm, v(-0.34, 17.28) * mm, v(-0.06, 17.22) * mm, v(-1.4, 15.54) * mm, v(-1.82, 15.44) * mm]});
            skFitSpline(sketch, "E112", {"points": [v(-1.51, 14) * mm, v(-1.5, 14.27) * mm, v(0.2, 16.23) * mm, v(0.47, 16.27) * mm, v(0.45, 16.02) * mm, v(-1.25, 14.06) * mm, v(-1.51, 14) * mm]});
            skFitSpline(sketch, "E113", {"points": [v(-0.64, 13.6) * mm, v(0.85, 15.42) * mm, v(1.14, 15.46) * mm, v(1.05, 15.28) * mm, v(-0.34, 13.64) * mm, v(-0.64, 13.6) * mm]});
            skFitSpline(sketch, "E114", {"points": [v(0.75, 17.64) * mm, v(1.01, 17.62) * mm, v(1.14, 17.12) * mm, v(1.8, 15.82) * mm, v(1.84, 15.58) * mm, v(1.14, 16.27) * mm, v(0.75, 17.64) * mm]});
            skFitSpline(sketch, "E115", {"points": [v(2.05, 19.66) * mm, v(1.7, 19.26) * mm, v(1.8, 18.23) * mm, v(2.43, 17.78) * mm, v(2.9, 17.82) * mm, v(2.73, 18.09) * mm, v(2.07, 18.4) * mm, v(1.98, 19.18) * mm, v(2.23, 19.54) * mm, v(2.05, 19.66) * mm]});
            skFitSpline(sketch, "E116", {"points": [v(6.94, -1.3) * mm, v(6.74, -1.05) * mm, v(7.04, -0.97) * mm, v(8.1, -1.45) * mm, v(8.77, -2.27) * mm, v(8.67, -2.4) * mm, v(8.15, -1.82) * mm, v(6.94, -1.3) * mm]});
            skFitSpline(sketch, "E117", {"points": [v(7.1, 0.03) * mm, v(7.28, 0.48) * mm, v(7.58, 0.68) * mm, v(7.66, 0.5) * mm, v(7.42, 0.2) * mm, v(7.4, -0.13) * mm, v(7.1, 0.03) * mm]});
            skFitSpline(sketch, "E118", {"points": [v(8.87, -3.05) * mm, v(8.97, -2.67) * mm, v(9.14, -3.02) * mm, v(8.87, -3.05) * mm]});
            skFitSpline(sketch, "E119", {"points": [v(9.55, -1.39) * mm, v(9.87, -1.45) * mm, v(10.08, -1.8) * mm, v(10.28, -1.75) * mm, v(10.1, -1.4) * mm, v(9.74, -1.12) * mm, v(9.55, -1.39) * mm]});
            skFitSpline(sketch, "E120", {"points": [v(10.6, -0.24) * mm, v(10.64, 0) * mm, v(11.14, 0.38) * mm, v(12.08, 1.9) * mm, v(12.24, 2.81) * mm, v(12.41, 2.96) * mm, v(12.55, 2.61) * mm, v(12, 0.97) * mm, v(11.07, -0.04) * mm, v(10.6, -0.24) * mm]});
            skFitSpline(sketch, "E121", {"points": [v(11.34, -0.73) * mm, v(11.38, -0.49) * mm, v(12, -0.53) * mm, v(12.54, -0.99) * mm, v(12.7, -1.26) * mm, v(12.42, -1.32) * mm, v(12.14, -0.87) * mm, v(11.34, -0.73) * mm]});
            skFitSpline(sketch, "E122", {"points": [v(12.88, 0.96) * mm, v(12.7, 1.08) * mm, v(13.22, 1.66) * mm, v(13.95, 3.14) * mm, v(14.17, 4.48) * mm, v(14.44, 4.57) * mm, v(14.5, 4.04) * mm, v(14.07, 2.54) * mm, v(12.88, 0.96) * mm]});
            skFitSpline(sketch, "E123", {"points": [v(14, 7.3) * mm, v(14.1, 8.1) * mm, v(13.85, 8.36) * mm, v(13.8, 8.62) * mm, v(14.28, 8.54) * mm, v(14.44, 7.75) * mm, v(14.28, 7.27) * mm, v(14, 7.3) * mm]});
            skFitSpline(sketch, "E124", {"points": [v(13.08, 8.3) * mm, v(12.78, 8.3) * mm, v(12.82, 7.86) * mm, v(13.04, 7.36) * mm, v(13.34, 7.48) * mm, v(13.3, 7.8) * mm, v(13.65, 7.67) * mm, v(13.56, 7.3) * mm, v(13.04, 6.98) * mm, v(12.47, 7.64) * mm, v(12.52, 8.41) * mm, v(13.12, 8.6) * mm, v(13.08, 8.3) * mm]});
            skFitSpline(sketch, "E125", {"points": [v(13.8, 0.72) * mm, v(13.6, 0.77) * mm, v(13.7, 0.96) * mm, v(14.69, 1.7) * mm, v(15.52, 2.8) * mm, v(15.74, 2.88) * mm, v(15.8, 2.71) * mm, v(14.9, 1.54) * mm, v(13.8, 0.72) * mm]});
            skFitSpline(sketch, "E126", {"points": [v(12.48, -0.11) * mm, v(12.36, 0.06) * mm, v(12.56, 0.28) * mm, v(13.34, 0.38) * mm, v(16.5, 1.37) * mm, v(19.04, 2.8) * mm, v(19.28, 2.88) * mm, v(19.28, 2.6) * mm, v(16.57, 1.15) * mm, v(13.38, 0.06) * mm, v(12.48, -0.11) * mm]});
            skFitSpline(sketch, "E127", {"points": [v(16.71, 0.43) * mm, v(16.44, 0.5) * mm, v(16.6, 0.69) * mm, v(17.7, 0.96) * mm, v(19.1, 0.65) * mm, v(19.97, 0.02) * mm, v(19.85, -0.14) * mm, v(19.41, 0.2) * mm, v(17.95, 0.65) * mm, v(16.71, 0.43) * mm]});
            skFitSpline(sketch, "E128", {"points": [v(19.65, 2.05) * mm, v(19.53, 1.9) * mm, v(19.67, 1.76) * mm, v(20.78, 2.55) * mm, v(21.5, 3.64) * mm, v(21.5, 3.96) * mm, v(21.35, 4.12) * mm, v(21.18, 4.02) * mm, v(21.22, 3.76) * mm, v(20.69, 2.75) * mm, v(19.65, 2.05) * mm]});
            skFitSpline(sketch, "E129", {"points": [v(21.8, 2.63) * mm, v(21.6, 2.75) * mm, v(21.73, 2.92) * mm, v(21.9, 2.83) * mm, v(23.15, 3.02) * mm, v(24.3, 3.96) * mm, v(24.4, 4.72) * mm, v(24.2, 5) * mm, v(24.03, 4.86) * mm, v(24.17, 4.58) * mm, v(24.1, 4.35) * mm, v(23.88, 4.43) * mm, v(23.73, 4.9) * mm, v(24.1, 5.27) * mm, v(24.57, 5) * mm, v(24.65, 4.08) * mm, v(23.4, 2.82) * mm, v(21.8, 2.63) * mm]});
            skFitSpline(sketch, "E130", {"points": [v(21.72, 0.67) * mm, v(21.5, 0.67) * mm, v(21.72, 0.96) * mm, v(23.01, 0.52) * mm, v(24.54, -1.09) * mm, v(24.88, -2.76) * mm, v(24.76, -3.5) * mm, v(24.6, -3.42) * mm, v(24.63, -2.76) * mm, v(24.34, -1.26) * mm, v(23.5, -0.16) * mm, v(22.55, 0.4) * mm, v(21.72, 0.67) * mm]});
            skFitSpline(sketch, "E131", {"points": [v(23.13, 1.07) * mm, v(22.96, 1.24) * mm, v(23.16, 1.3) * mm, v(24.6, 0.39) * mm, v(25.5, -1.53) * mm, v(25.29, -2.98) * mm, v(25.15, -2.9) * mm, v(25.17, -2.52) * mm, v(25.2, -1.45) * mm, v(24.4, 0.32) * mm, v(23.13, 1.07) * mm]});
            skFitSpline(sketch, "E132", {"points": [v(26.05, -1.77) * mm, v(25.85, -1.74) * mm, v(25.87, -1.92) * mm, v(26.78, -2.42) * mm, v(27.9, -2.1) * mm, v(27.9, -1.89) * mm, v(27.74, -1.89) * mm, v(26.94, -2.18) * mm, v(26.05, -1.77) * mm]});
            skFitSpline(sketch, "E133", {"points": [v(25.58, -3.75) * mm, v(25.68, -3.53) * mm, v(25.93, -3.69) * mm, v(25.93, -4.98) * mm, v(25.42, -6.01) * mm, v(24.57, -6.64) * mm, v(24.47, -6.47) * mm, v(24.8, -6.26) * mm, v(25.52, -5.43) * mm, v(25.83, -4.4) * mm, v(25.58, -3.75) * mm]});
            skFitSpline(sketch, "E134", {"points": [v(21.14, -6.52) * mm, v(21.4, -6.66) * mm, v(21.22, -6.78) * mm, v(20.91, -6.84) * mm, v(20.77, -7.53) * mm, v(21.74, -8.26) * mm, v(22.83, -8.08) * mm, v(23.14, -7.97) * mm, v(23.06, -8.28) * mm, v(22.23, -8.52) * mm, v(21.4, -8.44) * mm, v(20.47, -7.55) * mm, v(20.59, -6.84) * mm, v(21.14, -6.52) * mm]});
            skFitSpline(sketch, "E135", {"points": [v(21.4, -9.01) * mm, v(20.98, -9.04) * mm, v(21.34, -9.33) * mm, v(23.05, -9.68) * mm, v(25.23, -8.26) * mm, v(25.57, -7.76) * mm, v(25.37, -7.55) * mm, v(25, -8.08) * mm, v(23.71, -9.16) * mm, v(22.06, -9.36) * mm, v(21.4, -9.01) * mm]});
            skFitSpline(sketch, "E136", {"points": [v(19.57, -11.39) * mm, v(19.2, -11.53) * mm, v(19.54, -11.77) * mm, v(20.98, -11.64) * mm, v(22.2, -10.67) * mm, v(22.25, -10.4) * mm, v(21.97, -10.43) * mm, v(21.74, -10.82) * mm, v(20.7, -11.4) * mm, v(19.57, -11.39) * mm]});
            skFitSpline(sketch, "E137", {"points": [v(23.42, -10.96) * mm, v(23.18, -11.29) * mm, v(23.18, -12.04) * mm, v(23.67, -12.69) * mm, v(24.01, -12.93) * mm, v(24.08, -12.73) * mm, v(23.65, -12.37) * mm, v(23.42, -11.67) * mm, v(23.51, -11.19) * mm, v(23.42, -10.96) * mm]});
            skFitSpline(sketch, "E138", {"points": [v(21.75, -11.78) * mm, v(21.85, -12.01) * mm, v(21.38, -12.36) * mm, v(20.05, -13.77) * mm, v(19.12, -15.69) * mm, v(18.82, -16.74) * mm, v(18.62, -16.82) * mm, v(18.98, -15.38) * mm, v(19.93, -13.43) * mm, v(21.75, -11.78) * mm]});
            skFitSpline(sketch, "E139", {"points": [v(19.53, -17.02) * mm, v(19.45, -17.39) * mm, v(19.9, -18.19) * mm, v(20.62, -18.3) * mm, v(20.99, -17.82) * mm, v(20.76, -17.34) * mm, v(20.82, -17.2) * mm, v(21.19, -17.53) * mm, v(21.12, -18.07) * mm, v(20.47, -18.56) * mm, v(19.53, -18.16) * mm, v(19.23, -17.42) * mm, v(19.23, -16.96) * mm, v(19.53, -17.02) * mm]});
            skFitSpline(sketch, "E140", {"points": [v(-3.75, -7.3) * mm, v(-3.75, -7.38) * mm, v(-3.66, -7.38) * mm], "startDerivative": vector(-0.04, -0.2) * mm, "endDerivative": vector(0.2, 0.04) * mm});
            skFitSpline(sketch, "E141", {"points": [v(-26.47, -7.58) * mm, v(-26.59, -5.35) * mm], "startDerivative": vector(1.04, 1.67) * mm, "endDerivative": vector(-2.72, 4.24) * mm});
            skFitSpline(sketch, "E142", {"points": [v(-19.4, -5.96) * mm, v(-18.99, -5.69) * mm], "startDerivative": vector(0.09, -0.53) * mm, "endDerivative": vector(-0.04, 1.04) * mm});
            skSolve(sketch);
        }
        {
            var Q0;
            Q0=makeQuery(id+"F0.imprint","IMPRINT",FACE,{"disambiguationData":[TD([[makeQuery(id+"F0.imprint","IMPRINT",EDGE,{"derivedFrom":sQuery(id+"F0.wireOp",EDGE,"E70")}),1.0]])]});
            var Q1;
            Q1=makeQuery(id+"F0.imprint","IMPRINT",FACE,{"disambiguationData":[TD([[makeQuery(id+"F0.imprint","IMPRINT",EDGE,{"derivedFrom":sQuery(id+"F0.wireOp",EDGE,"E71")}),1.0]])]});
            var Q2;
            Q2=makeQuery(id+"F0.imprint","IMPRINT",FACE,{"disambiguationData":[TD([[makeQuery(id+"F0.imprint","IMPRINT",EDGE,{"derivedFrom":sQuery(id+"F0.wireOp",EDGE,"E72")}),-1.0]])]});
            var Q3;
            Q3=makeQuery(id+"F0.imprint","IMPRINT",FACE,{"disambiguationData":[TD([[makeQuery(id+"F0.imprint","IMPRINT",EDGE,{"derivedFrom":sQuery(id+"F0.wireOp",EDGE,"E74")}),-1.0]])]});
            var Q4;
            Q4=makeQuery(id+"F0.imprint","IMPRINT",FACE,{"disambiguationData":[TD([[makeQuery(id+"F0.imprint","IMPRINT",EDGE,{"derivedFrom":sQuery(id+"F0.wireOp",EDGE,"E87")}),-1.0]])]});
            var Q5;
            Q5=makeQuery(id+"F0.imprint","IMPRINT",FACE,{"disambiguationData":[TD([[makeQuery(id+"F0.imprint","IMPRINT",EDGE,{"derivedFrom":sQuery(id+"F0.wireOp",EDGE,"E75")}),1.0]])]});
            var Q6;
            Q6=makeQuery(id+"F0.imprint","IMPRINT",FACE,{"disambiguationData":[TD([[makeQuery(id+"F0.imprint","IMPRINT",EDGE,{"derivedFrom":sQuery(id+"F0.wireOp",EDGE,"E82")}),1.0]])]});
            var Q7;
            Q7=makeQuery(id+"F0.imprint","IMPRINT",FACE,{"disambiguationData":[TD([[makeQuery(id+"F0.imprint","IMPRINT",EDGE,{"derivedFrom":sQuery(id+"F0.wireOp",EDGE,"E81")}),1.0]])]});
            var Q8;
            Q8=makeQuery(id+"F0.imprint","IMPRINT",FACE,{"disambiguationData":[TD([[makeQuery(id+"F0.imprint","IMPRINT",EDGE,{"derivedFrom":sQuery(id+"F0.wireOp",EDGE,"E83")}),1.0]])]});
            var Q9;
            Q9=makeQuery(id+"F0.imprint","IMPRINT",FACE,{"disambiguationData":[TD([[makeQuery(id+"F0.imprint","IMPRINT",EDGE,{"derivedFrom":sQuery(id+"F0.wireOp",EDGE,"E85")}),-1.0]])]});
            var Q10;
            Q10=makeQuery(id+"F0.imprint","IMPRINT",FACE,{"disambiguationData":[TD([[makeQuery(id+"F0.imprint","IMPRINT",EDGE,{"derivedFrom":sQuery(id+"F0.wireOp",EDGE,"E86")}),-1.0]])]});
            var Q11;
            Q11=makeQuery(id+"F0.imprint","IMPRINT",FACE,{"disambiguationData":[TD([[makeQuery(id+"F0.imprint","IMPRINT",EDGE,{"derivedFrom":sQuery(id+"F0.wireOp",EDGE,"E84")}),-1.0]])]});
            var Q12;
            Q12=makeQuery(id+"F0.imprint","IMPRINT",FACE,{"disambiguationData":[TD([[makeQuery(id+"F0.imprint","IMPRINT",EDGE,{"derivedFrom":sQuery(id+"F0.wireOp",EDGE,"E111")}),-1.0]])]});
            var Q13;
            Q13=makeQuery(id+"F0.imprint","IMPRINT",FACE,{"disambiguationData":[TD([[makeQuery(id+"F0.imprint","IMPRINT",EDGE,{"derivedFrom":sQuery(id+"F0.wireOp",EDGE,"E112")}),-1.0]])]});
            var Q14;
            Q14=makeQuery(id+"F0.imprint","IMPRINT",FACE,{"disambiguationData":[TD([[makeQuery(id+"F0.imprint","IMPRINT",EDGE,{"derivedFrom":sQuery(id+"F0.wireOp",EDGE,"E113")}),-1.0]])]});
            var Q15;
            Q15=makeQuery(id+"F0.imprint","IMPRINT",FACE,{"disambiguationData":[TD([[makeQuery(id+"F0.imprint","IMPRINT",EDGE,{"derivedFrom":sQuery(id+"F0.wireOp",EDGE,"E114")}),-1.0]])]});
            var Q16;
            Q16=makeQuery(id+"F0.imprint","IMPRINT",FACE,{"disambiguationData":[TD([[makeQuery(id+"F0.imprint","IMPRINT",EDGE,{"derivedFrom":sQuery(id+"F0.wireOp",EDGE,"E115")}),1.0]])]});
            var Q17;
            Q17=makeQuery(id+"F0.imprint","IMPRINT",FACE,{"disambiguationData":[TD([[makeQuery(id+"F0.imprint","IMPRINT",EDGE,{"derivedFrom":sQuery(id+"F0.wireOp",EDGE,"E88")}),-1.0]])]});
            var Q18;
            Q18=makeQuery(id+"F0.imprint","IMPRINT",FACE,{"disambiguationData":[TD([[makeQuery(id+"F0.imprint","IMPRINT",EDGE,{"derivedFrom":sQuery(id+"F0.wireOp",EDGE,"E78")}),-1.0]])]});
            var Q19;
            Q19=makeQuery(id+"F0.imprint","IMPRINT",FACE,{"disambiguationData":[TD([[makeQuery(id+"F0.imprint","IMPRINT",EDGE,{"derivedFrom":sQuery(id+"F0.wireOp",EDGE,"E76")}),1.0]])]});
            var Q20;
            Q20=makeQuery(id+"F0.imprint","IMPRINT",FACE,{"disambiguationData":[TD([[makeQuery(id+"F0.imprint","IMPRINT",EDGE,{"derivedFrom":sQuery(id+"F0.wireOp",EDGE,"E77")}),1.0]])]});
            var Q21;
            Q21=makeQuery(id+"F0.imprint","IMPRINT",FACE,{"disambiguationData":[TD([[makeQuery(id+"F0.imprint","IMPRINT",EDGE,{"derivedFrom":sQuery(id+"F0.wireOp",EDGE,"E117")}),-1.0]])]});
            var Q22;
            Q22=makeQuery(id+"F0.imprint","IMPRINT",FACE,{"disambiguationData":[TD([[makeQuery(id+"F0.imprint","IMPRINT",EDGE,{"derivedFrom":sQuery(id+"F0.wireOp",EDGE,"E116")}),-1.0]])]});
            var Q23;
            Q23=makeQuery(id+"F0.imprint","IMPRINT",FACE,{"disambiguationData":[TD([[makeQuery(id+"F0.imprint","IMPRINT",EDGE,{"derivedFrom":sQuery(id+"F0.wireOp",EDGE,"E119")}),1.0]])]});
            var Q24;
            Q24=makeQuery(id+"F0.imprint","IMPRINT",FACE,{"disambiguationData":[TD([[makeQuery(id+"F0.imprint","IMPRINT",EDGE,{"derivedFrom":sQuery(id+"F0.wireOp",EDGE,"E121")}),-1.0]])]});
            var Q25;
            Q25=makeQuery(id+"F0.imprint","IMPRINT",FACE,{"disambiguationData":[TD([[makeQuery(id+"F0.imprint","IMPRINT",EDGE,{"derivedFrom":sQuery(id+"F0.wireOp",EDGE,"E120")}),-1.0]])]});
            var Q26;
            Q26=makeQuery(id+"F0.imprint","IMPRINT",FACE,{"disambiguationData":[TD([[makeQuery(id+"F0.imprint","IMPRINT",EDGE,{"derivedFrom":sQuery(id+"F0.wireOp",EDGE,"E122")}),-1.0]])]});
            var Q27;
            Q27=makeQuery(id+"F0.imprint","IMPRINT",FACE,{"disambiguationData":[TD([[makeQuery(id+"F0.imprint","IMPRINT",EDGE,{"derivedFrom":sQuery(id+"F0.wireOp",EDGE,"E125")}),-1.0]])]});
            var Q28;
            Q28=makeQuery(id+"F0.imprint","IMPRINT",FACE,{"disambiguationData":[TD([[makeQuery(id+"F0.imprint","IMPRINT",EDGE,{"derivedFrom":sQuery(id+"F0.wireOp",EDGE,"E126")}),-1.0]])]});
            var Q29;
            Q29=makeQuery(id+"F0.imprint","IMPRINT",FACE,{"disambiguationData":[TD([[makeQuery(id+"F0.imprint","IMPRINT",EDGE,{"derivedFrom":sQuery(id+"F0.wireOp",EDGE,"E80")}),-1.0]])]});
            var Q30;
            Q30=makeQuery(id+"F0.imprint","IMPRINT",FACE,{"disambiguationData":[TD([[makeQuery(id+"F0.imprint","IMPRINT",EDGE,{"derivedFrom":sQuery(id+"F0.wireOp",EDGE,"E79")}),-1.0]])]});
            var Q31;
            Q31=makeQuery(id+"F0.imprint","IMPRINT",FACE,{"disambiguationData":[TD([[makeQuery(id+"F0.imprint","IMPRINT",EDGE,{"derivedFrom":sQuery(id+"F0.wireOp",EDGE,"E124")}),-1.0]])]});
            var Q32;
            Q32=makeQuery(id+"F0.imprint","IMPRINT",FACE,{"disambiguationData":[TD([[makeQuery(id+"F0.imprint","IMPRINT",EDGE,{"derivedFrom":sQuery(id+"F0.wireOp",EDGE,"E123")}),-1.0]])]});
            var Q33;
            Q33=makeQuery(id+"F0.imprint","IMPRINT",FACE,{"disambiguationData":[TD([[makeQuery(id+"F0.imprint","IMPRINT",EDGE,{"derivedFrom":sQuery(id+"F0.wireOp",EDGE,"E118")}),-1.0]])]});
            var Q34;
            Q34=makeQuery(id+"F0.imprint","IMPRINT",FACE,{"disambiguationData":[TD([[makeQuery(id+"F0.imprint","IMPRINT",EDGE,{"derivedFrom":sQuery(id+"F0.wireOp",EDGE,"E127")}),-1.0]])]});
            var Q35;
            Q35=makeQuery(id+"F0.imprint","IMPRINT",FACE,{"disambiguationData":[TD([[makeQuery(id+"F0.imprint","IMPRINT",EDGE,{"derivedFrom":sQuery(id+"F0.wireOp",EDGE,"E128")}),1.0]])]});
            var Q36;
            Q36=makeQuery(id+"F0.imprint","IMPRINT",FACE,{"disambiguationData":[TD([[makeQuery(id+"F0.imprint","IMPRINT",EDGE,{"derivedFrom":sQuery(id+"F0.wireOp",EDGE,"E129")}),-1.0]])]});
            var Q37;
            Q37=makeQuery(id+"F0.imprint","IMPRINT",FACE,{"disambiguationData":[TD([[makeQuery(id+"F0.imprint","IMPRINT",EDGE,{"derivedFrom":sQuery(id+"F0.wireOp",EDGE,"E131")}),-1.0]])]});
            var Q38;
            Q38=makeQuery(id+"F0.imprint","IMPRINT",FACE,{"disambiguationData":[TD([[makeQuery(id+"F0.imprint","IMPRINT",EDGE,{"derivedFrom":sQuery(id+"F0.wireOp",EDGE,"E130")}),-1.0]])]});
            var Q39;
            Q39=makeQuery(id+"F0.imprint","IMPRINT",FACE,{"disambiguationData":[TD([[makeQuery(id+"F0.imprint","IMPRINT",EDGE,{"derivedFrom":sQuery(id+"F0.wireOp",EDGE,"E132")}),1.0]])]});
            var Q40;
            Q40=makeQuery(id+"F0.imprint","IMPRINT",FACE,{"disambiguationData":[TD([[makeQuery(id+"F0.imprint","IMPRINT",EDGE,{"derivedFrom":sQuery(id+"F0.wireOp",EDGE,"E133")}),-1.0]])]});
            var Q41;
            Q41=makeQuery(id+"F0.imprint","IMPRINT",FACE,{"disambiguationData":[TD([[makeQuery(id+"F0.imprint","IMPRINT",EDGE,{"derivedFrom":sQuery(id+"F0.wireOp",EDGE,"E134")}),-1.0]])]});
            var Q42;
            Q42=makeQuery(id+"F0.imprint","IMPRINT",FACE,{"disambiguationData":[TD([[makeQuery(id+"F0.imprint","IMPRINT",EDGE,{"derivedFrom":sQuery(id+"F0.wireOp",EDGE,"E135")}),1.0]])]});
            var Q43;
            Q43=makeQuery(id+"F0.imprint","IMPRINT",FACE,{"disambiguationData":[TD([[makeQuery(id+"F0.imprint","IMPRINT",EDGE,{"derivedFrom":sQuery(id+"F0.wireOp",EDGE,"E136")}),1.0]])]});
            var Q44;
            Q44=makeQuery(id+"F0.imprint","IMPRINT",FACE,{"disambiguationData":[TD([[makeQuery(id+"F0.imprint","IMPRINT",EDGE,{"derivedFrom":sQuery(id+"F0.wireOp",EDGE,"E137")}),1.0]])]});
            var Q45;
            Q45=makeQuery(id+"F0.imprint","IMPRINT",FACE,{"disambiguationData":[TD([[makeQuery(id+"F0.imprint","IMPRINT",EDGE,{"derivedFrom":sQuery(id+"F0.wireOp",EDGE,"E138")}),-1.0]])]});
            var Q46;
            Q46=makeQuery(id+"F0.imprint","IMPRINT",FACE,{"disambiguationData":[TD([[makeQuery(id+"F0.imprint","IMPRINT",EDGE,{"derivedFrom":sQuery(id+"F0.wireOp",EDGE,"E139")}),-1.0]])]});
            var Q47;
            Q47=makeQuery(id+"F0.imprint","IMPRINT",FACE,{"disambiguationData":[TD([[makeQuery(id+"F0.imprint","IMPRINT",EDGE,{"derivedFrom":sQuery(id+"F0.wireOp",EDGE,"E92")}),1.0]])]});
            var Q48;
            Q48=makeQuery(id+"F0.imprint","IMPRINT",FACE,{"disambiguationData":[TD([[makeQuery(id+"F0.imprint","IMPRINT",EDGE,{"derivedFrom":sQuery(id+"F0.wireOp",EDGE,"E94")}),-1.0]])]});
            var Q49;
            Q49=makeQuery(id+"F0.imprint","IMPRINT",FACE,{"disambiguationData":[TD([[makeQuery(id+"F0.imprint","IMPRINT",EDGE,{"derivedFrom":sQuery(id+"F0.wireOp",EDGE,"E91")}),-1.0]])]});
            var Q50;
            Q50=makeQuery(id+"F0.imprint","IMPRINT",FACE,{"disambiguationData":[TD([[makeQuery(id+"F0.imprint","IMPRINT",EDGE,{"derivedFrom":sQuery(id+"F0.wireOp",EDGE,"E90")}),-1.0]])]});
            var Q51;
            Q51=makeQuery(id+"F0.imprint","IMPRINT",FACE,{"disambiguationData":[TD([[makeQuery(id+"F0.imprint","IMPRINT",EDGE,{"derivedFrom":sQuery(id+"F0.wireOp",EDGE,"E89")}),-1.0]])]});
            var Q52;
            Q52=makeQuery(id+"F0.imprint","IMPRINT",FACE,{"disambiguationData":[TD([[makeQuery(id+"F0.imprint","IMPRINT",EDGE,{"derivedFrom":sQuery(id+"F0.wireOp",EDGE,"E95")}),1.0]])]});
            var Q53;
            Q53=makeQuery(id+"F0.imprint","IMPRINT",FACE,{"disambiguationData":[TD([[makeQuery(id+"F0.imprint","IMPRINT",EDGE,{"derivedFrom":sQuery(id+"F0.wireOp",EDGE,"E96")}),-1.0]])]});
            var Q54;
            Q54=makeQuery(id+"F0.imprint","IMPRINT",FACE,{"disambiguationData":[TD([[makeQuery(id+"F0.imprint","IMPRINT",EDGE,{"derivedFrom":sQuery(id+"F0.wireOp",EDGE,"E93")}),-1.0]])]});
            var Q55;
            Q55=makeQuery(id+"F0.imprint","IMPRINT",FACE,{"disambiguationData":[TD([[makeQuery(id+"F0.imprint","IMPRINT",EDGE,{"derivedFrom":sQuery(id+"F0.wireOp",EDGE,"E109")}),1.0]])]});
            var Q56;
            Q56=makeQuery(id+"F0.imprint","IMPRINT",FACE,{"disambiguationData":[TD([[makeQuery(id+"F0.imprint","IMPRINT",EDGE,{"derivedFrom":sQuery(id+"F0.wireOp",EDGE,"E108")}),-1.0]])]});
            var Q57;
            Q57=makeQuery(id+"F0.imprint","IMPRINT",FACE,{"disambiguationData":[TD([[makeQuery(id+"F0.imprint","IMPRINT",EDGE,{"derivedFrom":sQuery(id+"F0.wireOp",EDGE,"E110")}),1.0]])]});
            var Q58;
            Q58=makeQuery(id+"F0.imprint","IMPRINT",FACE,{"disambiguationData":[TD([[makeQuery(id+"F0.imprint","IMPRINT",EDGE,{"derivedFrom":sQuery(id+"F0.wireOp",EDGE,"E106")}),-1.0]])]});
            var Q59;
            Q59=makeQuery(id+"F0.imprint","IMPRINT",FACE,{"disambiguationData":[TD([[makeQuery(id+"F0.imprint","IMPRINT",EDGE,{"derivedFrom":sQuery(id+"F0.wireOp",EDGE,"E107")}),1.0]])]});
            var Q60;
            Q60=makeQuery(id+"F0.imprint","IMPRINT",FACE,{"disambiguationData":[TD([[makeQuery(id+"F0.imprint","IMPRINT",EDGE,{"derivedFrom":sQuery(id+"F0.wireOp",EDGE,"E105")}),-1.0]])]});
            var Q61;
            Q61=makeQuery(id+"F0.imprint","IMPRINT",FACE,{"disambiguationData":[TD([[makeQuery(id+"F0.imprint","IMPRINT",EDGE,{"derivedFrom":sQuery(id+"F0.wireOp",EDGE,"E104")}),-1.0]])]});
            var Q62;
            Q62=makeQuery(id+"F0.imprint","IMPRINT",FACE,{"disambiguationData":[TD([[makeQuery(id+"F0.imprint","IMPRINT",EDGE,{"derivedFrom":sQuery(id+"F0.wireOp",EDGE,"E103")}),-1.0]])]});
            var Q63;
            Q63=makeQuery(id+"F0.imprint","IMPRINT",FACE,{"disambiguationData":[TD([[makeQuery(id+"F0.imprint","IMPRINT",EDGE,{"derivedFrom":sQuery(id+"F0.wireOp",EDGE,"E101")}),-1.0]])]});
            var Q64;
            Q64=makeQuery(id+"F0.imprint","IMPRINT",FACE,{"disambiguationData":[TD([[makeQuery(id+"F0.imprint","IMPRINT",EDGE,{"derivedFrom":sQuery(id+"F0.wireOp",EDGE,"E102")}),-1.0]])]});
            var Q65;
            Q65=makeQuery(id+"F0.imprint","IMPRINT",FACE,{"disambiguationData":[TD([[makeQuery(id+"F0.imprint","IMPRINT",EDGE,{"derivedFrom":sQuery(id+"F0.wireOp",EDGE,"E100")}),1.0]])]});
            var Q66;
            Q66=makeQuery(id+"F0.imprint","IMPRINT",FACE,{"disambiguationData":[TD([[makeQuery(id+"F0.imprint","IMPRINT",EDGE,{"derivedFrom":sQuery(id+"F0.wireOp",EDGE,"E99")}),1.0]])]});
            var Q67;
            Q67=makeQuery(id+"F0.imprint","IMPRINT",FACE,{"disambiguationData":[TD([[makeQuery(id+"F0.imprint","IMPRINT",EDGE,{"derivedFrom":sQuery(id+"F0.wireOp",EDGE,"E97")}),1.0]])]});
            var Q68;
            Q68=makeQuery(id+"F0.imprint","IMPRINT",FACE,{"disambiguationData":[TD([[makeQuery(id+"F0.imprint","IMPRINT",EDGE,{"derivedFrom":sQuery(id+"F0.wireOp",EDGE,"E98")}),-1.0]])]});
            var Q69;
            {var subQ0=sQuery(id+"F0.wireOp",EDGE,"E142");var subQ1=sQuery(id+"F0.wireOp",EDGE,"E107");var subQ2=makeQuery(id+"F0.imprint","INTERSECT",VERTEX,{"disambiguationData":[OD(0.0)],"derivedFrom":[subQ1,subQ0]});Q69=makeQuery(id+"F0.imprint","IMPRINT",FACE,{"disambiguationData":[TD([[makeQuery(id+"F0.imprint","IMPRINT",EDGE,{"disambiguationData":[TD([[subQ2,1.0]])],"derivedFrom":subQ1}),-1.0]])]});}
            extrude(context, id + "F1", {"entities" : qUnion([Q0, Q1, Q2, Q3, Q4, Q5, Q6, Q7, Q8, Q9, Q10, Q11, Q12, Q13, Q14, Q15, Q16, Q17, Q18, Q19, Q20, Q21, Q22, Q23, Q24, Q25, Q26, Q27, Q28, Q29, Q30, Q31, Q32, Q33, Q34, Q35, Q36, Q37, Q38, Q39, Q40, Q41, Q42, Q43, Q44, Q45, Q46, Q47, Q48, Q49, Q50, Q51, Q52, Q53, Q54, Q55, Q56, Q57, Q58, Q59, Q60, Q61, Q62, Q63, Q64, Q65, Q66, Q67, Q68, Q69]), "depth" : 0.77 * mm});
        }
        {
            var Q0;
            Q0=makeQuery(id+"F0.imprint","IMPRINT",FACE,{"disambiguationData":[TD([[makeQuery(id+"F0.imprint","IMPRINT",EDGE,{"derivedFrom":sQuery(id+"F0.wireOp",EDGE,"E0")}),-1.0]])]});
            var Q1;
            {var subQ0=sQuery(id+"F0.wireOp",EDGE,"E141");var subQ1=sQuery(id+"F0.wireOp",EDGE,"E68");var subQ2=makeQuery(id+"F0.imprint","INTERSECT",VERTEX,{"disambiguationData":[OD(0.0)],"derivedFrom":[subQ1,subQ0]});Q1=makeQuery(id+"F0.imprint","IMPRINT",FACE,{"disambiguationData":[TD([[makeQuery(id+"F0.imprint","IMPRINT",EDGE,{"disambiguationData":[TD([[subQ2,-1.0]])],"derivedFrom":subQ1}),1.0]])]});}
            extrude(context, id + "F2", {"entities" : qUnion([Q0, Q1]), "operationType" : NewBodyOperationType.ADD, "depth" : 0.77 * mm});
        }
        {
            var Q0;
            Q0=makeQuery(id+"F1.opExtrude","SWEPT_BODY",BODY,{"disambiguationData":[OSD([sQuery(id+"F0.wireOp",EDGE,"E70")])]});
            var Q1;
            Q1=makeQuery(id+"F1.opExtrude","SWEPT_BODY",BODY,{"disambiguationData":[OSD([sQuery(id+"F0.wireOp",EDGE,"E71")])]});
            var Q2;
            Q2=makeQuery(id+"F1.opExtrude","SWEPT_BODY",BODY,{"disambiguationData":[OSD([sQuery(id+"F0.wireOp",EDGE,"E74")])]});
            var Q3;
            Q3=makeQuery(id+"F1.opExtrude","SWEPT_BODY",BODY,{"disambiguationData":[OSD([sQuery(id+"F0.wireOp",EDGE,"E75")])]});
            var Q4;
            Q4=makeQuery(id+"F1.opExtrude","SWEPT_BODY",BODY,{"disambiguationData":[OSD([sQuery(id+"F0.wireOp",EDGE,"E76")])]});
            var Q5;
            Q5=makeQuery(id+"F1.opExtrude","SWEPT_BODY",BODY,{"disambiguationData":[OSD([sQuery(id+"F0.wireOp",EDGE,"E77")])]});
            var Q6;
            Q6=makeQuery(id+"F1.opExtrude","SWEPT_BODY",BODY,{"disambiguationData":[OSD([sQuery(id+"F0.wireOp",EDGE,"E78")])]});
            var Q7;
            Q7=makeQuery(id+"F1.opExtrude","SWEPT_BODY",BODY,{"disambiguationData":[OSD([sQuery(id+"F0.wireOp",EDGE,"E79")])]});
            var Q8;
            Q8=makeQuery(id+"F1.opExtrude","SWEPT_BODY",BODY,{"disambiguationData":[OSD([sQuery(id+"F0.wireOp",EDGE,"E80")])]});
            var Q9;
            Q9=makeQuery(id+"F1.opExtrude","SWEPT_BODY",BODY,{"disambiguationData":[OSD([sQuery(id+"F0.wireOp",EDGE,"E81")])]});
            var Q10;
            Q10=makeQuery(id+"F1.opExtrude","SWEPT_BODY",BODY,{"disambiguationData":[OSD([sQuery(id+"F0.wireOp",EDGE,"E82")])]});
            var Q11;
            Q11=makeQuery(id+"F1.opExtrude","SWEPT_BODY",BODY,{"disambiguationData":[OSD([sQuery(id+"F0.wireOp",EDGE,"E83")])]});
            var Q12;
            Q12=makeQuery(id+"F1.opExtrude","SWEPT_BODY",BODY,{"disambiguationData":[OSD([sQuery(id+"F0.wireOp",EDGE,"E84")])]});
            var Q13;
            Q13=makeQuery(id+"F1.opExtrude","SWEPT_BODY",BODY,{"disambiguationData":[OSD([sQuery(id+"F0.wireOp",EDGE,"E85")])]});
            var Q14;
            Q14=makeQuery(id+"F1.opExtrude","SWEPT_BODY",BODY,{"disambiguationData":[OSD([sQuery(id+"F0.wireOp",EDGE,"E86")])]});
            var Q15;
            Q15=makeQuery(id+"F1.opExtrude","SWEPT_BODY",BODY,{"disambiguationData":[OSD([sQuery(id+"F0.wireOp",EDGE,"E87")])]});
            var Q16;
            Q16=makeQuery(id+"F1.opExtrude","SWEPT_BODY",BODY,{"disambiguationData":[OSD([sQuery(id+"F0.wireOp",EDGE,"E88")])]});
            var Q17;
            Q17=makeQuery(id+"F1.opExtrude","SWEPT_BODY",BODY,{"disambiguationData":[OSD([sQuery(id+"F0.wireOp",EDGE,"E89")])]});
            var Q18;
            Q18=makeQuery(id+"F1.opExtrude","SWEPT_BODY",BODY,{"disambiguationData":[OSD([sQuery(id+"F0.wireOp",EDGE,"E90")])]});
            var Q19;
            Q19=makeQuery(id+"F1.opExtrude","SWEPT_BODY",BODY,{"disambiguationData":[OSD([sQuery(id+"F0.wireOp",EDGE,"E91")])]});
            var Q20;
            Q20=makeQuery(id+"F1.opExtrude","SWEPT_BODY",BODY,{"disambiguationData":[OSD([sQuery(id+"F0.wireOp",EDGE,"E92")])]});
            var Q21;
            Q21=makeQuery(id+"F1.opExtrude","SWEPT_BODY",BODY,{"disambiguationData":[OSD([sQuery(id+"F0.wireOp",EDGE,"E93")])]});
            var Q22;
            Q22=makeQuery(id+"F1.opExtrude","SWEPT_BODY",BODY,{"disambiguationData":[OSD([sQuery(id+"F0.wireOp",EDGE,"E94")])]});
            var Q23;
            Q23=makeQuery(id+"F1.opExtrude","SWEPT_BODY",BODY,{"disambiguationData":[OSD([sQuery(id+"F0.wireOp",EDGE,"E95")])]});
            var Q24;
            Q24=makeQuery(id+"F1.opExtrude","SWEPT_BODY",BODY,{"disambiguationData":[OSD([sQuery(id+"F0.wireOp",EDGE,"E96")])]});
            var Q25;
            Q25=makeQuery(id+"F1.opExtrude","SWEPT_BODY",BODY,{"disambiguationData":[OSD([sQuery(id+"F0.wireOp",EDGE,"E97")])]});
            var Q26;
            Q26=makeQuery(id+"F1.opExtrude","SWEPT_BODY",BODY,{"disambiguationData":[OSD([sQuery(id+"F0.wireOp",EDGE,"E98")])]});
            var Q27;
            Q27=makeQuery(id+"F1.opExtrude","SWEPT_BODY",BODY,{"disambiguationData":[OSD([sQuery(id+"F0.wireOp",EDGE,"E99")])]});
            var Q28;
            Q28=makeQuery(id+"F1.opExtrude","SWEPT_BODY",BODY,{"disambiguationData":[OSD([sQuery(id+"F0.wireOp",EDGE,"E100")])]});
            var Q29;
            Q29=makeQuery(id+"F1.opExtrude","SWEPT_BODY",BODY,{"disambiguationData":[OSD([sQuery(id+"F0.wireOp",EDGE,"E101")])]});
            var Q30;
            Q30=makeQuery(id+"F1.opExtrude","SWEPT_BODY",BODY,{"disambiguationData":[OSD([sQuery(id+"F0.wireOp",EDGE,"E102")])]});
            var Q31;
            Q31=makeQuery(id+"F1.opExtrude","SWEPT_BODY",BODY,{"disambiguationData":[OSD([sQuery(id+"F0.wireOp",EDGE,"E103")])]});
            var Q32;
            Q32=makeQuery(id+"F1.opExtrude","SWEPT_BODY",BODY,{"disambiguationData":[OSD([sQuery(id+"F0.wireOp",EDGE,"E104")])]});
            var Q33;
            Q33=makeQuery(id+"F1.opExtrude","SWEPT_BODY",BODY,{"disambiguationData":[OSD([sQuery(id+"F0.wireOp",EDGE,"E105")])]});
            var Q34;
            Q34=makeQuery(id+"F1.opExtrude","SWEPT_BODY",BODY,{"disambiguationData":[OSD([sQuery(id+"F0.wireOp",EDGE,"E106")])]});
            var Q35;
            Q35=makeQuery(id+"F1.opExtrude","SWEPT_BODY",BODY,{"disambiguationData":[OSD([sQuery(id+"F0.wireOp",EDGE,"E107")])]});
            var Q36;
            Q36=makeQuery(id+"F1.opExtrude","SWEPT_BODY",BODY,{"disambiguationData":[OSD([sQuery(id+"F0.wireOp",EDGE,"E108")])]});
            var Q37;
            Q37=makeQuery(id+"F1.opExtrude","SWEPT_BODY",BODY,{"disambiguationData":[OSD([sQuery(id+"F0.wireOp",EDGE,"E109")])]});
            var Q38;
            Q38=makeQuery(id+"F1.opExtrude","SWEPT_BODY",BODY,{"disambiguationData":[OSD([sQuery(id+"F0.wireOp",EDGE,"E110")])]});
            var Q39;
            Q39=makeQuery(id+"F1.opExtrude","SWEPT_BODY",BODY,{"disambiguationData":[OSD([sQuery(id+"F0.wireOp",EDGE,"E111")])]});
            var Q40;
            Q40=makeQuery(id+"F1.opExtrude","SWEPT_BODY",BODY,{"disambiguationData":[OSD([sQuery(id+"F0.wireOp",EDGE,"E112")])]});
            var Q41;
            Q41=makeQuery(id+"F1.opExtrude","SWEPT_BODY",BODY,{"disambiguationData":[OSD([sQuery(id+"F0.wireOp",EDGE,"E113")])]});
            var Q42;
            Q42=makeQuery(id+"F1.opExtrude","SWEPT_BODY",BODY,{"disambiguationData":[OSD([sQuery(id+"F0.wireOp",EDGE,"E114")])]});
            var Q43;
            Q43=makeQuery(id+"F1.opExtrude","SWEPT_BODY",BODY,{"disambiguationData":[OSD([sQuery(id+"F0.wireOp",EDGE,"E115")])]});
            var Q44;
            Q44=makeQuery(id+"F1.opExtrude","SWEPT_BODY",BODY,{"disambiguationData":[OSD([sQuery(id+"F0.wireOp",EDGE,"E116")])]});
            var Q45;
            Q45=makeQuery(id+"F1.opExtrude","SWEPT_BODY",BODY,{"disambiguationData":[OSD([sQuery(id+"F0.wireOp",EDGE,"E117")])]});
            var Q46;
            Q46=makeQuery(id+"F1.opExtrude","SWEPT_BODY",BODY,{"disambiguationData":[OSD([sQuery(id+"F0.wireOp",EDGE,"E118")])]});
            var Q47;
            Q47=makeQuery(id+"F1.opExtrude","SWEPT_BODY",BODY,{"disambiguationData":[OSD([sQuery(id+"F0.wireOp",EDGE,"E119")])]});
            var Q48;
            Q48=makeQuery(id+"F1.opExtrude","SWEPT_BODY",BODY,{"disambiguationData":[OSD([sQuery(id+"F0.wireOp",EDGE,"E120")])]});
            var Q49;
            Q49=makeQuery(id+"F1.opExtrude","SWEPT_BODY",BODY,{"disambiguationData":[OSD([sQuery(id+"F0.wireOp",EDGE,"E121")])]});
            var Q50;
            Q50=makeQuery(id+"F1.opExtrude","SWEPT_BODY",BODY,{"disambiguationData":[OSD([sQuery(id+"F0.wireOp",EDGE,"E122")])]});
            var Q51;
            Q51=makeQuery(id+"F1.opExtrude","SWEPT_BODY",BODY,{"disambiguationData":[OSD([sQuery(id+"F0.wireOp",EDGE,"E123")])]});
            var Q52;
            Q52=makeQuery(id+"F1.opExtrude","SWEPT_BODY",BODY,{"disambiguationData":[OSD([sQuery(id+"F0.wireOp",EDGE,"E124")])]});
            var Q53;
            Q53=makeQuery(id+"F1.opExtrude","SWEPT_BODY",BODY,{"disambiguationData":[OSD([sQuery(id+"F0.wireOp",EDGE,"E125")])]});
            var Q54;
            Q54=makeQuery(id+"F1.opExtrude","SWEPT_BODY",BODY,{"disambiguationData":[OSD([sQuery(id+"F0.wireOp",EDGE,"E126")])]});
            var Q55;
            Q55=makeQuery(id+"F1.opExtrude","SWEPT_BODY",BODY,{"disambiguationData":[OSD([sQuery(id+"F0.wireOp",EDGE,"E127")])]});
            var Q56;
            Q56=makeQuery(id+"F1.opExtrude","SWEPT_BODY",BODY,{"disambiguationData":[OSD([sQuery(id+"F0.wireOp",EDGE,"E128")])]});
            var Q57;
            Q57=makeQuery(id+"F1.opExtrude","SWEPT_BODY",BODY,{"disambiguationData":[OSD([sQuery(id+"F0.wireOp",EDGE,"E129")])]});
            var Q58;
            Q58=makeQuery(id+"F1.opExtrude","SWEPT_BODY",BODY,{"disambiguationData":[OSD([sQuery(id+"F0.wireOp",EDGE,"E130")])]});
            var Q59;
            Q59=makeQuery(id+"F1.opExtrude","SWEPT_BODY",BODY,{"disambiguationData":[OSD([sQuery(id+"F0.wireOp",EDGE,"E131")])]});
            var Q60;
            Q60=makeQuery(id+"F1.opExtrude","SWEPT_BODY",BODY,{"disambiguationData":[OSD([sQuery(id+"F0.wireOp",EDGE,"E132")])]});
            var Q61;
            Q61=makeQuery(id+"F1.opExtrude","SWEPT_BODY",BODY,{"disambiguationData":[OSD([sQuery(id+"F0.wireOp",EDGE,"E133")])]});
            var Q62;
            Q62=makeQuery(id+"F1.opExtrude","SWEPT_BODY",BODY,{"disambiguationData":[OSD([sQuery(id+"F0.wireOp",EDGE,"E134")])]});
            var Q63;
            Q63=makeQuery(id+"F1.opExtrude","SWEPT_BODY",BODY,{"disambiguationData":[OSD([sQuery(id+"F0.wireOp",EDGE,"E135")])]});
            var Q64;
            Q64=makeQuery(id+"F1.opExtrude","SWEPT_BODY",BODY,{"disambiguationData":[OSD([sQuery(id+"F0.wireOp",EDGE,"E136")])]});
            var Q65;
            Q65=makeQuery(id+"F1.opExtrude","SWEPT_BODY",BODY,{"disambiguationData":[OSD([sQuery(id+"F0.wireOp",EDGE,"E137")])]});
            var Q66;
            Q66=makeQuery(id+"F1.opExtrude","SWEPT_BODY",BODY,{"disambiguationData":[OSD([sQuery(id+"F0.wireOp",EDGE,"E138")])]});
            var Q67;
            Q67=makeQuery(id+"F1.opExtrude","SWEPT_BODY",BODY,{"disambiguationData":[OSD([sQuery(id+"F0.wireOp",EDGE,"E139")])]});
            var Q68;
            Q68=makeQuery(id+"F1.opExtrude","SWEPT_BODY",BODY,{"disambiguationData":[OSD([sQuery(id+"F0.wireOp",EDGE,"E72"),sQuery(id+"F0.wireOp",EDGE,"E73")])]});
            booleanBodies(context, id + "F3", {"operationType" : BooleanOperationType.SUBTRACTION, "tools" : qUnion([Q0, Q1, Q2, Q3, Q4, Q5, Q6, Q7, Q8, Q9, Q10, Q11, Q12, Q13, Q14, Q15, Q16, Q17, Q18, Q19, Q20, Q21, Q22, Q23, Q24, Q25, Q26, Q27, Q28, Q29, Q30, Q31, Q32, Q33, Q34, Q35, Q36, Q37, Q38, Q39, Q40, Q41, Q42, Q43, Q44, Q45, Q46, Q47, Q48, Q49, Q50, Q51, Q52, Q53, Q54, Q55, Q56, Q57, Q58, Q59, Q60, Q61, Q62, Q63, Q64, Q65, Q66, Q67]), "targets" : qUnion([Q68])});
        }
        {
            var Q0;
            Q0=makeQuery(id+"F1.opExtrude","SWEPT_BODY",BODY,{"disambiguationData":[OSD([sQuery(id+"F0.wireOp",EDGE,"E72"),sQuery(id+"F0.wireOp",EDGE,"E73")])]});
            var Q1;
            Q1=qCreatedBy(makeId("Origin.pointOp"),VERTEX);
            transform(context, id + "F4", {"entities" : qUnion([Q0]), "transformType" : TransformType.SCALE_UNIFORMLY, "scale" : 2.6, "scalePoint" : qUnion([Q1]), "makeCopy" : false});
        }
    });
